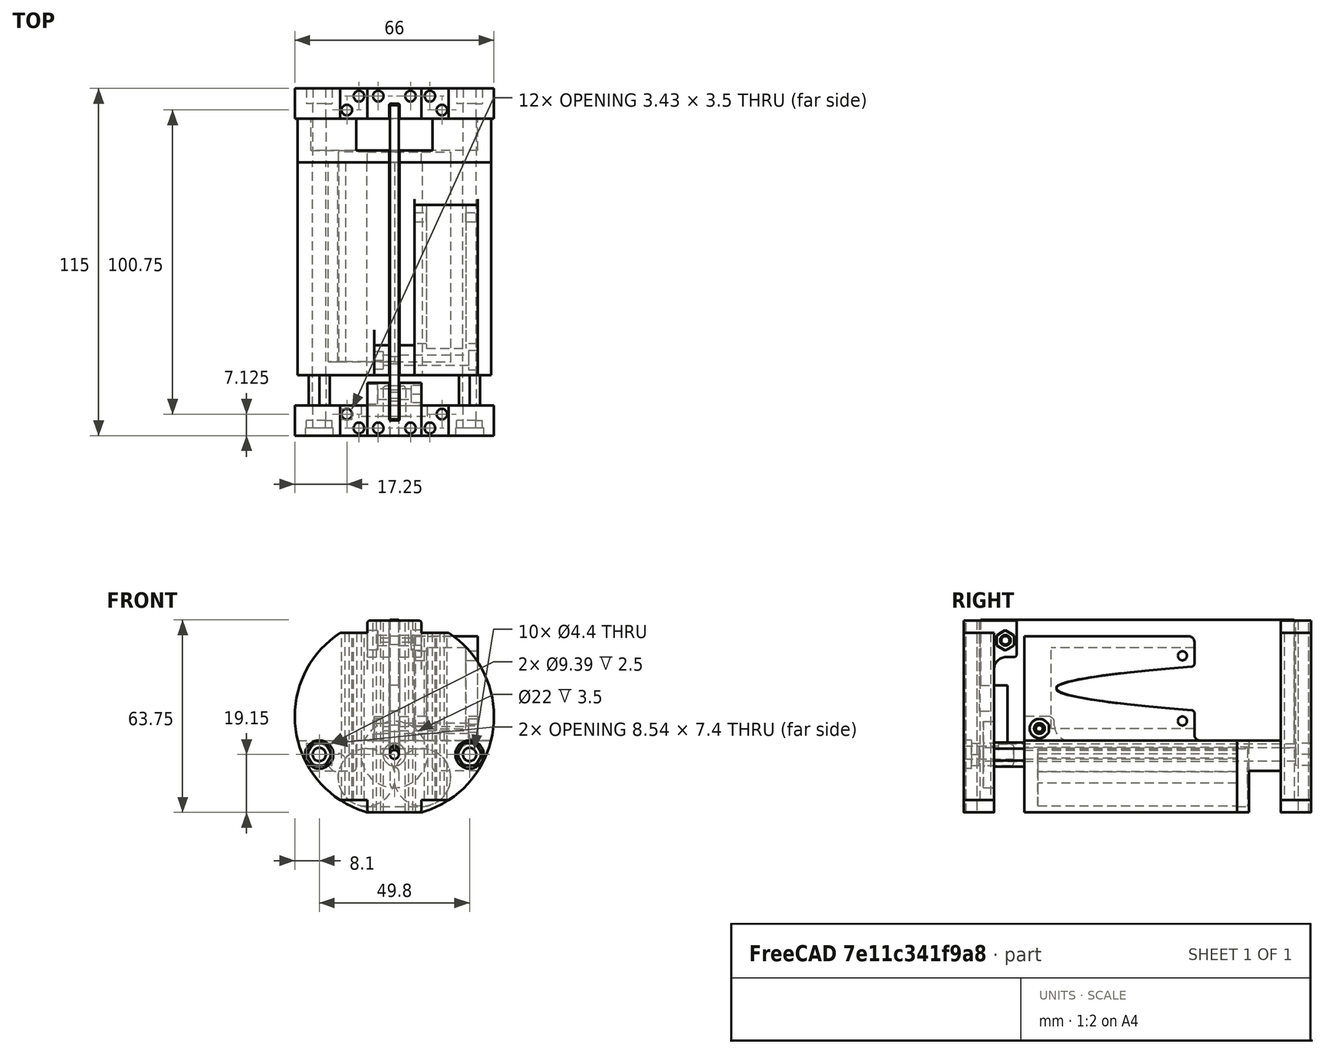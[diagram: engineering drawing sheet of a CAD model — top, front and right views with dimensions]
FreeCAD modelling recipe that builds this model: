
FCSTD DOCUMENT  (FreeCAD 0.19R24366 (Git))
Label: Corte_piezas_DEF_4
License: Creative Commons Attribution-ShareAlike
LicenseURL: http://creativecommons.org/licenses/by-sa/4.0/
objects: Sketcher::SketchObject×38, PartDesign::Pocket×24, PartDesign::Pad×14, PartDesign::Fillet×14, TechDraw::DrawViewBalloon×14, PartDesign::ShapeBinder×8, TechDraw::DrawViewPart×8, PartDesign::Body×7, PartDesign::Mirrored×5, TechDraw::DrawViewDimension×5, Part::Refine×3, TechDraw::DrawSVGTemplate×3, TechDraw::DrawPage×3, TechDraw::DrawProjGroupItem×2, Spreadsheet::Sheet×1, PartDesign::MultiTransform×1, App::DocumentObjectGroup×1, TechDraw::DrawProjGroup×1
note: 166 computed .brp shape members not serialized (recipe doc carries the construction recipe); baked Part::Feature solids carry a one-line shape summary decoded from their .brp

FEATURE [Spreadsheet::Sheet] Spreadsheet  label="Datos"
  cells = A1=Diámetro pila; B1(DiametroPila)=18.5; A2=Tolerancia; B2(tolerancia)=0.4; A3=Largo Pila; B3(largoPila)=65; A4=Separacion; B4(separacion)=1; A5=Grosor tapa; B5(grosortapa)=4.5; A6=Largo Bote; B6(LargoBote)=115; A7= Rosca pasante Diámetro; B7(roscaPasante4)=4; A8=Ancho placa electrónica; B8(anchoPlaca)=3; A9=Diámetro tornillos placa; B9(tornillosParaLaPlaca)=3; A10=GrosorGPS; B10(GPSgrosor)=12.5; A11=AnchoGPS; B11(GPSancho)=26.2; A12=AltoGPS; B12(GPSAlto)=36; A13=Ancho tuerca de 3; B13(anchoTuercaExterior)=5.4
FEATURE [Sketcher::SketchObject] Sketch  label="habitaculo_pila_antena"
  FullyConstrained = true
  MapMode = 5
  Placement = pos=(0,0,0) rot=(1,0,0;1.5708rad)
  Support = -> [XZ_Plane]
  expr: Constraints[7] = <<Datos>>.tolerancia + <<Datos>>.roscaPasante4
  expr: Constraints[2] = <<Datos>>.DiametroPila + <<Datos>>.tolerancia
  expr: Constraints[15] = <<Datos>>.DiametroPila
  sketch-geometry (13):
    g0: Circle CenterX=0 CenterY=0 CenterZ=0 NormalX=0 NormalY=0 NormalZ=1 AngleXU=0 Radius=33
    g1: LineSegment StartX=-9.25 StartY=-31.6771 StartZ=0 EndX=9.25 EndY=-31.6771 EndZ=0
    g2: LineSegment StartX=-32.0156 StartY=-8 StartZ=0 EndX=32.0156 EndY=-8 EndZ=0
    g3: ArcOfCircle CenterX=-9.25 CenterY=-20.1771 CenterZ=0 NormalX=0 NormalY=0 NormalZ=1 AngleXU=0 Radius=9.45 StartAngle=0.206102 EndAngle=2.40475
    g4: ArcOfCircle CenterX=9.25 CenterY=-20.1771 CenterZ=0 NormalX=0 NormalY=0 NormalZ=1 AngleXU=0 Radius=9.45 StartAngle=3.3477 EndAngle=9.21868
    g5: Circle CenterX=24.9 CenterY=-12.6 CenterZ=0 NormalX=0 NormalY=0 NormalZ=1 AngleXU=0 Radius=2.2
    g6: ArcOfCircle CenterX=0 CenterY=0 CenterZ=0 NormalX=0 NormalY=0 NormalZ=1 AngleXU=0 Radius=33 StartAngle=3.38646 EndAngle=4.42828
    g7: ArcOfCircle CenterX=0 CenterY=0 CenterZ=0 NormalX=0 NormalY=0 NormalZ=1 AngleXU=0 Radius=33 StartAngle=4.9965 EndAngle=6.03832
    g8: ArcOfCircle CenterX=-18.8935 CenterY=-15.243 CenterZ=0 NormalX=0 NormalY=0 NormalZ=1 AngleXU=0 Radius=3 StartAngle=0.491509 EndAngle=4.84582
    g9: ArcOfCircle CenterX=-9.25 CenterY=-20.1771 CenterZ=0 NormalX=0 NormalY=0 NormalZ=1 AngleXU=0 Radius=9.45 StartAngle=2.93258 EndAngle=6.07708
    g10: Circle CenterX=-24.9 CenterY=-12.6 CenterZ=0 NormalX=0 NormalY=0 NormalZ=1 AngleXU=0 Radius=2.2
    g11: Circle CenterX=0 CenterY=-12.6 CenterZ=0 NormalX=0 NormalY=0 NormalZ=1 AngleXU=0 Radius=1.45
    g12: LineSegment StartX=24.9 StartY=-12.6 StartZ=0 EndX=0 EndY=-12.6 EndZ=0
  constraints (38):
    c: Diameter(g0) = 66
    c: Horizontal(g1)
    c: Diameter(g3) = 18.9
    c: Equal(g3,g4)
    c: Coincident(g4,g9)
    c: Coincident(g4,g3)
    c: Coincident(g0,g-1)
    c: Diameter(g5) = 4.4
    c: Horizontal(g2)
    c: Vertical(g1,g4)
    c: Coincident(g6,g-1)
    c: Coincident(g6,g1)
    c: Coincident(g7,g6)
    c: Coincident(g7,g1)
    c: Symmetric(g4,g3,g-2)
    c: DistanceX(g3,g4) = 18.5
    c: PointOnObject(g1,g0)
    c: DistanceY(g1,g3) = 11.5
    c: DistanceY(g2,g6) = 8
    c: PointOnObject(g6,g0)
    c: Coincident(g2,g6)
    c: Coincident(g7,g2)
    c: Equal(g3,g9)
    c: Coincident(g3,g8)
    c: Coincident(g9,g8)
    c: Coincident(g3,g9)
    c: Radius(g8) = 3
    c: DistanceX(g8,g2) = -13.1222
    c: DistanceY(g8,g2) = 7.24297
    c: Symmetric(g10,g5,g-2)
    c: Equal(g10,g5)
    c: Diameter(g11) = 2.9  'Antena'
    c: Coincident(g12,g5)
    c: Coincident(g12,g11)
    c: Horizontal(g12)
    c: PointOnObject(g11,g-2)
    c: DistanceY(g5,g2) = 4.6
    c: DistanceX(g11,g5) = 24.9
FEATURE [PartDesign::Pad] Pad  label="habitaculo_Pila"
  Direction = (1,1,1)
  Length = 66
  Length2 = 100
  Midplane = true
  Placement = pos=(0,0,0) rot=(1,0,0;1.5708rad)
  Profile = -> Sketch
  Type = 0
  expr: Length = <<Datos>>.largoPila + <<Datos>>.separacion
FEATURE [PartDesign::ShapeBinder] ShapeBinder003
  Placement = pos=(0,-4.5,-1e-15) rot=(0,0,1;0rad)
  TraceSupport = false
FEATURE [Sketcher::SketchObject] Sketch022  label="Sketch_placa"
  ExternalGeometry = -> [ShapeBinder003]
  FullyConstrained = true
  Placement = pos=(0,0,-3.7e-14) rot=(0,0.707107,0.707107;3.14159rad)
  Support = -> [ShapeBinder003]
  expr: Constraints[8] = <<Datos>>.anchoPlaca
  sketch-geometry (4):
    g0: LineSegment StartX=-1.5 StartY=32 StartZ=0 EndX=1.5 EndY=32 EndZ=0
    g1: LineSegment StartX=1.5 StartY=32 StartZ=0 EndX=1.5 EndY=-9 EndZ=0
    g2: LineSegment StartX=1.5 StartY=-9 StartZ=0 EndX=-1.5 EndY=-9 EndZ=0
    g3: LineSegment StartX=-1.5 StartY=-9 StartZ=0 EndX=-1.5 EndY=32 EndZ=0
  constraints (11):
    c: Coincident(g0,g1)
    c: Coincident(g1,g2)
    c: Coincident(g2,g3)
    c: Coincident(g3,g0)
    c: Horizontal(g2)
    c: Vertical(g1)
    c: Vertical(g3)
    c: Symmetric(g0,g0,g-2)
    c: DistanceX(g0,g0) = 3
    c: DistanceY(g1,g1) = 41
    c: DistanceY(g-3,g0) = 40
FEATURE [PartDesign::Pad] Pad009  label="Placa_electrónica"
  Direction = (1,1,1)
  Length = 104
  Length2 = 100
  Midplane = true
  Placement = pos=(0,-4.5,-1e-15) rot=(0,0,1;0rad)
  Profile = -> Sketch022
  Type = 0
FEATURE [Sketcher::SketchObject] Sketch023
  ExternalGeometry = -> [Pad009]
  FullyConstrained = true
  MapMode = 5
  Placement = pos=(0,-52,5.17e-14) rot=(1,0,0;1.5708rad)
  Support = -> [Pad009]
  sketch-geometry (4):
    g0: LineSegment StartX=-1.5 StartY=-9 StartZ=0 EndX=1.5 EndY=-9 EndZ=0
    g1: LineSegment StartX=1.5 StartY=-9 StartZ=0 EndX=1.5 EndY=10.3 EndZ=0
    g2: LineSegment StartX=1.5 StartY=10.3 StartZ=0 EndX=-1.5 EndY=10.3 EndZ=0
    g3: LineSegment StartX=-1.5 StartY=10.3 StartZ=0 EndX=-1.5 EndY=-9 EndZ=0
  constraints (11):
    c: Coincident(g0,g1)
    c: Coincident(g1,g2)
    c: Coincident(g2,g3)
    c: Coincident(g3,g0)
    c: Horizontal(g0)
    c: Horizontal(g2)
    c: Vertical(g1)
    c: Vertical(g3)
    c: Coincident(g0,g-3)
    c: PointOnObject(g1,g-4)
    c: DistanceY(g1,g1) = 19.3
FEATURE [PartDesign::Pocket] Pocket011
  BaseFeature = -> Pad009
  Length = 9
  Length2 = 100
  Placement = pos=(0,-4.5,-1e-15) rot=(0,0,1;0rad)
  Profile = -> Sketch023
  Type = 0
FEATURE [PartDesign::ShapeBinder] ShapeBinder
  Placement = pos=(0,-4.5,-1e-15) rot=(0,0,1;0rad)
  TraceSupport = false
FEATURE [Sketcher::SketchObject] Sketch024  label="Forma_pasante1"
  ExternalGeometry = -> [ShapeBinder]
  FullyConstrained = true
  MapMode = 5
  Placement = pos=(0,-37.5,-1.19e-14) rot=(1,0,0;1.5708rad)
  Support = -> [ShapeBinder]
  sketch-geometry (8):
    g0: Circle CenterX=24.9 CenterY=-12.6 CenterZ=0 NormalX=0 NormalY=0 NormalZ=1 AngleXU=0 Radius=2.2
    g1: LineSegment StartX=28.3641 StartY=-14.6 StartZ=0 EndX=28.3641 EndY=-10.6 EndZ=0
    g2: LineSegment StartX=28.3641 StartY=-10.6 StartZ=0 EndX=24.9 EndY=-8.6 EndZ=0
    g3: LineSegment StartX=24.9 StartY=-8.6 StartZ=0 EndX=21.4359 EndY=-10.6 EndZ=0
    g4: LineSegment StartX=21.4359 StartY=-10.6 StartZ=0 EndX=21.4359 EndY=-14.6 EndZ=0
    g5: LineSegment StartX=21.4359 StartY=-14.6 StartZ=0 EndX=24.9 EndY=-16.6 EndZ=0
    g6: LineSegment StartX=24.9 StartY=-16.6 StartZ=0 EndX=28.3641 EndY=-14.6 EndZ=0
    g7: Circle CenterX=24.9 CenterY=-12.6 CenterZ=0 NormalX=0 NormalY=0 NormalZ=1 AngleXU=0 Radius=4
  constraints (18):
    c: Coincident(g0,g-3)
    c: Equal(g0,g-3)
    c: Coincident(g1,g2)
    c: Coincident(g2,g3)
    c: Coincident(g3,g4)
    c: Coincident(g4,g5)
    c: Coincident(g5,g6)
    c: Coincident(g6,g1)
    c: Equal(g1, g2-g6) x5
    c: PointOnObject(g1,g7)
    c: PointOnObject(g2,g7)
    c: PointOnObject(g3,g7)
    c: PointOnObject(g4,g7)
    c: PointOnObject(g5,g7)
    c: PointOnObject(g6,g7)
    c: Coincident(g7,g0)
    c: Vertical(g1)
    c: Distance(g2) = 4
FEATURE [PartDesign::Pad] Pad010
  Direction = (1,1,1)
  Length = 10
  Length2 = 100
  Placement = pos=(0,-4.5,-1e-15) rot=(0,0,1;0rad)
  Profile = -> Sketch024
  Type = 0
FEATURE [PartDesign::Body] Body004  label="Pasante1"
  Group = -> [ShapeBinder,Sketch024,Pad010]
  Origin = -> Origin004
  Tip = -> Pad010
FEATURE [PartDesign::ShapeBinder] ShapeBinder004
  Placement = pos=(0,-10,-2.2e-15) rot=(0,0,1;0rad)
  Support = -> [Pad010]
  TraceSupport = false
FEATURE [Sketcher::SketchObject] Sketch025
  ExternalGeometry = -> [ShapeBinder004]
  FullyConstrained = true
  MapMode = 5
  Placement = pos=(0,-47.5,-2.43e-14) rot=(1,0,0;1.5708rad)
  Support = -> [ShapeBinder004]
  sketch-geometry (8):
    g0: Circle CenterX=24.9 CenterY=-12.6 CenterZ=0 NormalX=0 NormalY=0 NormalZ=1 AngleXU=0 Radius=2.2
    g1: LineSegment StartX=28.3641 StartY=-10.6 StartZ=0 EndX=24.9 EndY=-8.6 EndZ=0
    g2: LineSegment StartX=24.9 StartY=-8.6 StartZ=0 EndX=21.4359 EndY=-10.6 EndZ=0
    g3: LineSegment StartX=21.4359 StartY=-10.6 StartZ=0 EndX=21.4359 EndY=-14.6 EndZ=0
    g4: LineSegment StartX=21.4359 StartY=-14.6 StartZ=0 EndX=24.9 EndY=-16.6 EndZ=0
    g5: LineSegment StartX=24.9 StartY=-16.6 StartZ=0 EndX=28.3641 EndY=-14.6 EndZ=0
    g6: LineSegment StartX=28.3641 StartY=-14.6 StartZ=0 EndX=28.3641 EndY=-10.6 EndZ=0
    g7: Circle CenterX=24.9 CenterY=-12.6 CenterZ=0 NormalX=0 NormalY=0 NormalZ=1 AngleXU=0 Radius=4
  constraints (17):
    c: Coincident(g0,g-5)
    c: PointOnObject(g-4,g0)
    c: Coincident(g1,g2)
    c: Coincident(g2,g3)
    c: Coincident(g3,g4)
    c: Coincident(g4,g5)
    c: Coincident(g5,g6)
    c: Coincident(g6,g1)
    c: Equal(g1, g2-g6) x5
    c: PointOnObject(g1,g7)
    c: PointOnObject(g2,g7)
    c: PointOnObject(g3,g7)
    c: PointOnObject(g4,g7)
    c: PointOnObject(g5,g7)
    c: PointOnObject(g6,g7)
    c: Coincident(g7,g0)
    c: Coincident(g6,g-3)
FEATURE [PartDesign::Pad] Pad011
  Direction = (1,1,1)
  Length = 10
  Length2 = 100
  Placement = pos=(0,-10,-2.2e-15) rot=(0,0,1;0rad)
  Profile = -> Sketch025
  Type = 0
FEATURE [PartDesign::Body] Body005  label="Pasante2"
  Group = -> [ShapeBinder004,Sketch025,Pad011]
  Origin = -> Origin005
  Placement = pos=(-49.8,10,1.8e-15) rot=(0,0,1;0rad)
  Tip = -> Pad011
FEATURE [PartDesign::ShapeBinder] ShapeBinder005
  Placement = pos=(0,-4.5,-1e-15) rot=(0,0,1;0rad)
  TraceSupport = false
FEATURE [Sketcher::SketchObject] Sketch026
  ExternalGeometry = -> [ShapeBinder005]
  FullyConstrained = true
  Placement = pos=(0,-47.5,0) rot=(1,0,0;1.5708rad)
  Support = -> [ShapeBinder005]
  sketch-geometry (26):
    g0: ArcOfCircle CenterX=0 CenterY=0 CenterZ=0 NormalX=0 NormalY=0 NormalZ=1 AngleXU=0 Radius=33 StartAngle=5.28932 EndAngle=7.27705
    g1: LineSegment StartX=-9 StartY=-31.749 StartZ=0 EndX=9 EndY=-31.749 EndZ=0
    g2: LineSegment StartX=-9 StartY=31.749 StartZ=0 EndX=9 EndY=31.749 EndZ=0
    g3: ArcOfCircle CenterX=0 CenterY=0 CenterZ=0 NormalX=0 NormalY=0 NormalZ=1 AngleXU=0 Radius=33 StartAngle=2.14773 EndAngle=4.13546
    g4: ArcOfCircle CenterX=0 CenterY=-12.6 CenterZ=0 NormalX=0 NormalY=0 NormalZ=1 AngleXU=0 Radius=1.45 StartAngle=3.14159 EndAngle=6.28319
    g5: ArcOfCircle CenterX=1e-16 CenterY=-11.15 CenterZ=0 NormalX=0 NormalY=0 NormalZ=1 AngleXU=0 Radius=1.45 StartAngle=0 EndAngle=3.14159
    g6: LineSegment StartX=1.45 StartY=-12.6 StartZ=0 EndX=1.45 EndY=-11.15 EndZ=0
    g7: LineSegment StartX=-1.45 StartY=-12.6 StartZ=0 EndX=-1.45 EndY=-11.15 EndZ=0
    g8: LineSegment StartX=-18 StartY=27.6586 StartZ=0 EndX=-18 EndY=-27.6586 EndZ=0
    g9: LineSegment StartX=18 StartY=27.6586 StartZ=0 EndX=18 EndY=-27.6586 EndZ=0
    g10: LineSegment StartX=27.0362 StartY=-16.3 StartZ=0 EndX=29.1724 EndY=-12.6 EndZ=0
    g11: LineSegment StartX=29.1724 StartY=-12.6 StartZ=0 EndX=27.0362 EndY=-8.9 EndZ=0
    g12: LineSegment StartX=27.0362 StartY=-8.9 StartZ=0 EndX=22.7638 EndY=-8.9 EndZ=0
    g13: LineSegment StartX=22.7638 StartY=-8.9 StartZ=0 EndX=20.6276 EndY=-12.6 EndZ=0
    g14: LineSegment StartX=20.6276 StartY=-12.6 StartZ=0 EndX=22.7638 EndY=-16.3 EndZ=0
    g15: LineSegment StartX=22.7638 StartY=-16.3 StartZ=0 EndX=27.0362 EndY=-16.3 EndZ=0
    g16: Circle CenterX=24.9 CenterY=-12.6 CenterZ=0 NormalX=0 NormalY=0 NormalZ=1 AngleXU=0 Radius=4.27239
    g17: LineSegment StartX=22.7638 StartY=-8.9 StartZ=0 EndX=29.1724 EndY=-12.6 EndZ=0
    g18: LineSegment StartX=-18 StartY=27.6586 StartZ=0 EndX=-9 EndY=27.6586 EndZ=0
    g19: LineSegment StartX=-9 StartY=31.749 StartZ=0 EndX=-9 EndY=27.6586 EndZ=0
    g20: LineSegment StartX=-18 StartY=-27.6586 StartZ=0 EndX=-9 EndY=-27.6586 EndZ=0
    g21: LineSegment StartX=-9 StartY=-31.749 StartZ=0 EndX=-9 EndY=-27.6586 EndZ=0
    g22: LineSegment StartX=9 StartY=31.749 StartZ=0 EndX=9 EndY=27.6586 EndZ=0
    g23: LineSegment StartX=18 StartY=27.6586 StartZ=0 EndX=9 EndY=27.6586 EndZ=0
    g24: LineSegment StartX=9 StartY=-31.749 StartZ=0 EndX=9 EndY=-27.6586 EndZ=0
    g25: LineSegment StartX=18 StartY=-27.6586 StartZ=0 EndX=9 EndY=-27.6586 EndZ=0
  constraints (65):
    c: Coincident(g0,g-1)
    c: Coincident(g1,g-4)
    c: PointOnObject(g2,g0)
    c: Horizontal(g2)
    c: Equal(g0,g3)
    c: Coincident(g0,g3)
    c: Tangent(g4,g7) = 1.5708
    c: Tangent(g4,g6) = -1.5708
    c: Tangent(g6,g5) = -1.5708
    c: Tangent(g7,g5) = 1.5708
    c: Vertical(g6)
    c: Equal(g4,g5)
    c: Coincident(g4,g-6)
    c: PointOnObject(g4,g-6)
    c: PointOnObject(g5,g-6)
    c: Vertical(g8)
    c: Vertical(g9)
    c: Coincident(g10,g11)
    c: Coincident(g11,g12)
    c: Coincident(g12,g13)
    c: Coincident(g13,g14)
    c: Coincident(g14,g15)
    c: Coincident(g15,g10)
    c: Equal(g10, g11-g15) x5
    c: PointOnObject(g10,g16)
    c: PointOnObject(g11,g16)
    c: PointOnObject(g12,g16)
    c: PointOnObject(g13,g16)
    c: PointOnObject(g14,g16)
    c: PointOnObject(g15,g16)
    c: Coincident(g16,g-7)
    c: Coincident(g17,g12)
    c: Coincident(g17,g10)
    c: Distance(g17) = 7.4
    c: Horizontal(g15)
    c: Coincident(g19,g2)
    c: Coincident(g19,g18)
    c: Vertical(g19)
    c: Horizontal(g18)
    c: Coincident(g3,g8)
    c: Coincident(g20,g8)
    c: Coincident(g21,g1)
    c: Coincident(g21,g20)
    c: Vertical(g21)
    c: Horizontal(g20)
    c: Coincident(g3,g8)
    c: Vertical(g22)
    c: Coincident(g23,g9)
    c: Coincident(g23,g22)
    c: Coincident(g24,g1)
    c: Vertical(g24)
    c: Coincident(g25,g9)
    c: Coincident(g25,g24)
    c: Horizontal(g25)
    c: Horizontal(g23)
    c: Coincident(g0,g9)
    c: Coincident(g0,g9)
    c: Equal(g23,g18)
    c: Equal(g20,g25)
    c: Equal(g25,g23)
    c: Coincident(g22,g2)
    c: Coincident(g18,g3)
    c: PointOnObject(g0,g-3)
    c: Coincident(g1,g-3)
    c: DistanceX(g23,g23) = 9
FEATURE [PartDesign::Pad] Pad012  label="Cuerpo_principal"
  Direction = (1,1,1)
  Length = 10
  Length2 = 100
  Placement = pos=(0,-4.5,-1e-15) rot=(0,0,1;0rad)
  Profile = -> Sketch026
  Type = 0
FEATURE [Sketcher::SketchObject] Sketch027
  ExternalGeometry = -> [Pad012]
  FullyConstrained = true
  MapMode = 5
  Placement = pos=(0,-4.5,31.749) rot=(0,0,1;0rad)
  Support = -> [Pad012]
  sketch-geometry (4):
    g0: LineSegment StartX=-1.7 StartY=-48 StartZ=0 EndX=1.7 EndY=-48 EndZ=0
    g1: LineSegment StartX=1.7 StartY=-48 StartZ=0 EndX=1.7 EndY=-43 EndZ=0
    g2: LineSegment StartX=1.7 StartY=-43 StartZ=0 EndX=-1.7 EndY=-43 EndZ=0
    g3: LineSegment StartX=-1.7 StartY=-43 StartZ=0 EndX=-1.7 EndY=-48 EndZ=0
  constraints (11):
    c: Coincident(g0,g1)
    c: Coincident(g1,g2)
    c: Coincident(g2,g3)
    c: Coincident(g3,g0)
    c: Horizontal(g0)
    c: Vertical(g1)
    c: Vertical(g3)
    c: PointOnObject(g1,g-4)
    c: Symmetric(g1,g2,g-2)
    c: DistanceX(g0,g0) = 3.4
    c: DistanceY(g1,g1) = 5
FEATURE [PartDesign::Pocket] Pocket  label="Ranura_placa"
  BaseFeature = -> Pad012
  Length = 30
  Length2 = 100
  Placement = pos=(0,-4.5,-1e-15) rot=(0,0,1;0rad)
  Profile = -> Sketch027
  Type = 0
FEATURE [Sketcher::SketchObject] Sketch028  label="SK_agujeros_pasantes_paracaidas"
  ExternalGeometry = -> [Pocket]
  FullyConstrained = true
  MapMode = 5
  Placement = pos=(0,-4.5,31.749) rot=(0,0,1;0rad)
  Support = -> [Pocket]
  sketch-geometry (14):
    g0: LineSegment StartX=-1.7 StartY=-48 StartZ=0 EndX=-9 EndY=-48 EndZ=0
    g1: LineSegment StartX=-1.7 StartY=-48 StartZ=0 EndX=-9 EndY=-53 EndZ=0
    g2: LineSegment StartX=-6.07487 StartY=-48.75 StartZ=0 EndX=-4.62513 EndY=-48.75 EndZ=0
    g3: ArcOfCircle CenterX=-5.35 CenterY=-50.5 CenterZ=0 NormalX=0 NormalY=0 NormalZ=1 AngleXU=0 Radius=1.75 StartAngle=2.35619 EndAngle=7.06858
    g4: LineSegment StartX=-6.07487 StartY=-48.75 StartZ=0 EndX=-6.58744 EndY=-49.2626 EndZ=0
    g5: LineSegment StartX=-4.11256 StartY=-49.2626 StartZ=0 EndX=-4.62513 EndY=-48.75 EndZ=0
    g6: LineSegment StartX=-6.58744 StartY=-49.2626 StartZ=0 EndX=-4.11256 EndY=-49.2626 EndZ=0
    g7: Circle CenterX=-5.35 CenterY=-50.5 CenterZ=0 NormalX=0 NormalY=0 NormalZ=1 AngleXU=0 Radius=1.75
    g8: LineSegment StartX=4.62513 StartY=-48.75 StartZ=0 EndX=6.07487 EndY=-48.75 EndZ=0
    g9: ArcOfCircle CenterX=5.35 CenterY=-50.5 CenterZ=0 NormalX=0 NormalY=0 NormalZ=1 AngleXU=0 Radius=1.75 StartAngle=2.35619 EndAngle=7.06858
    g10: LineSegment StartX=4.62513 StartY=-48.75 StartZ=0 EndX=4.11256 EndY=-49.2626 EndZ=0
    g11: LineSegment StartX=6.58744 StartY=-49.2626 StartZ=0 EndX=6.07487 EndY=-48.75 EndZ=0
    g12: LineSegment StartX=4.11256 StartY=-49.2626 StartZ=0 EndX=6.58744 EndY=-49.2626 EndZ=0
    g13: Circle CenterX=5.35 CenterY=-50.5 CenterZ=0 NormalX=0 NormalY=0 NormalZ=1 AngleXU=0 Radius=1.75
  constraints (33):
    c: Coincident(g0,g-8)
    c: PointOnObject(g0,g-3)
    c: Horizontal(g0)
    c: Coincident(g1,g0)
    c: Coincident(g1,g-3)
    c: Horizontal(g2)
    c: Coincident(g4,g2)
    c: Coincident(g5,g2)
    c: Coincident(g6,g3)
    c: Horizontal(g6)
    c: Tangent(g4,g3) = -1.5708
    c: Tangent(g5,g3) = -1.5708
    c: Angle(g6,g4) = 0.785398
    c: Diameter(g3) = 3.5
    c: Symmetric(g0,g1,g3)
    c: Coincident(g7,g3)
    c: PointOnObject(g3,g7)
    c: Tangent(g7,g2)
    c: Coincident(g3,g6)
    c: Horizontal(g8)
    c: Coincident(g10,g8)
    c: Coincident(g11,g8)
    c: Coincident(g12,g9)
    c: Horizontal(g12)
    c: Tangent(g10,g9) = -1.5708
    c: Tangent(g11,g9) = -1.5708
    c: Angle(g12,g10) = 0.785398
    c: Equal(g3,g9) = 3.5
    c: Coincident(g13,g9)
    c: PointOnObject(g9,g13)
    c: Tangent(g13,g8)
    c: Coincident(g9,g12)
    c: Symmetric(g9,g3,g-2)
FEATURE [PartDesign::Pocket] Pocket012  label="agujeros_pasantes_paracaidas"
  BaseFeature = -> Pocket
  Length = 5
  Length2 = 100
  Placement = pos=(0,-4.5,-1e-15) rot=(0,0,1;0rad)
  Profile = -> Sketch028
  Type = 1
FEATURE [Sketcher::SketchObject] Sketch029
  ExternalGeometry = -> [Pocket012]
  FullyConstrained = true
  MapMode = 5
  Placement = pos=(0,-47.5,8.5e-15) rot=(0,0.707107,0.707107;3.14159rad)
  Support = -> [Pocket012]
  sketch-geometry (2):
    g0: Circle CenterX=0 CenterY=-12.6 CenterZ=0 NormalX=0 NormalY=0 NormalZ=1 AngleXU=0 Radius=11
    g1: Circle CenterX=0 CenterY=-12.6 CenterZ=0 NormalX=0 NormalY=0 NormalZ=1 AngleXU=0 Radius=4
  constraints (4):
    c: Coincident(g0,g-3)
    c: Diameter(g0) = 22
    c: Coincident(g1,g0)
    c: Diameter(g1) = 8
FEATURE [PartDesign::Pocket] Pocket013  label="Arandela_GND"
  BaseFeature = -> Pocket012
  Length = 3.5
  Length2 = 100
  Placement = pos=(0,-4.5,-1e-15) rot=(0,0,1;0rad)
  Profile = -> Sketch029
  Type = 0
FEATURE [Sketcher::SketchObject] Sketch030
  ExternalGeometry = -> [ShapeBinder005]
  FullyConstrained = true
  MapMode = 5
  Placement = pos=(0,-57.5,1.07e-14) rot=(1,0,0;1.5708rad)
  Support = -> [Pocket013]
  sketch-geometry (15):
    g0: LineSegment StartX=27.0362 StartY=-16.3 StartZ=0 EndX=29.1724 EndY=-12.6 EndZ=0
    g1: LineSegment StartX=29.1724 StartY=-12.6 StartZ=0 EndX=27.0362 EndY=-8.9 EndZ=0
    g2: LineSegment StartX=27.0362 StartY=-8.9 StartZ=0 EndX=22.7638 EndY=-8.9 EndZ=0
    g3: LineSegment StartX=22.7638 StartY=-8.9 StartZ=0 EndX=20.6276 EndY=-12.6 EndZ=0
    g4: LineSegment StartX=20.6276 StartY=-12.6 StartZ=0 EndX=22.7638 EndY=-16.3 EndZ=0
    g5: LineSegment StartX=22.7638 StartY=-16.3 StartZ=0 EndX=27.0362 EndY=-16.3 EndZ=0
    g6: Circle CenterX=24.9 CenterY=-12.6 CenterZ=0 NormalX=0 NormalY=0 NormalZ=1 AngleXU=0 Radius=4.27239
    g7: LineSegment StartX=-22.7638 StartY=-16.3 StartZ=0 EndX=-20.6276 EndY=-12.6 EndZ=0
    g8: LineSegment StartX=-20.6276 StartY=-12.6 StartZ=0 EndX=-22.7638 EndY=-8.9 EndZ=0
    g9: LineSegment StartX=-22.7638 StartY=-8.9 StartZ=0 EndX=-27.0362 EndY=-8.9 EndZ=0
    g10: LineSegment StartX=-27.0362 StartY=-8.9 StartZ=0 EndX=-29.1724 EndY=-12.6 EndZ=0
    g11: LineSegment StartX=-29.1724 StartY=-12.6 StartZ=0 EndX=-27.0362 EndY=-16.3 EndZ=0
    g12: LineSegment StartX=-27.0362 StartY=-16.3 StartZ=0 EndX=-22.7638 EndY=-16.3 EndZ=0
    g13: Circle CenterX=-24.9 CenterY=-12.6 CenterZ=0 NormalX=0 NormalY=0 NormalZ=1 AngleXU=0 Radius=4.27239
    g14: LineSegment StartX=22.7638 StartY=-8.9 StartZ=0 EndX=29.1724 EndY=-12.6 EndZ=0
  constraints (34):
    c: Coincident(g0,g1)
    c: Coincident(g1,g2)
    c: Coincident(g2,g3)
    c: Coincident(g3,g4)
    c: Coincident(g4,g5)
    c: Coincident(g5,g0)
    c: Equal(g0, g1-g5) x5
    c: PointOnObject(g0,g6)
    c: PointOnObject(g1,g6)
    c: PointOnObject(g2,g6)
    c: PointOnObject(g3,g6)
    c: PointOnObject(g4,g6)
    c: PointOnObject(g5,g6)
    c: Coincident(g6,g-3)
    c: Coincident(g7,g8)
    c: Coincident(g8,g9)
    c: Coincident(g9,g10)
    c: Coincident(g10,g11)
    c: Coincident(g11,g12)
    c: Coincident(g12,g7)
    c: Equal(g7, g8-g12) x5
    c: PointOnObject(g7,g13)
    c: PointOnObject(g8,g13)
    c: PointOnObject(g9,g13)
    c: PointOnObject(g10,g13)
    c: PointOnObject(g11,g13)
    c: PointOnObject(g12,g13)
    c: Coincident(g13,g-4)
    c: Coincident(g14,g2)
    c: Distance(g14) = 7.4
    c: Horizontal(g5)
    c: Coincident(g14,g0)
    c: Equal(g2,g9)
    c: Horizontal(g12)
FEATURE [PartDesign::Pocket] Pocket014  label="Encastro_tuercas"
  BaseFeature = -> Pocket013
  Length = 5
  Length2 = 100
  Placement = pos=(0,-4.5,-1e-15) rot=(0,0,1;0rad)
  Profile = -> Sketch030
  Type = 0
FEATURE [Sketcher::SketchObject] Sketch031
  ExternalGeometry = -> [Pocket014]
  FullyConstrained = true
  MapMode = 5
  Placement = pos=(0,-52.5,4.51e-14) rot=(1,0,0;1.5708rad)
  Support = -> [Pocket014]
  sketch-geometry (3):
    g0: Circle CenterX=24.9 CenterY=-12.6 CenterZ=0 NormalX=0 NormalY=0 NormalZ=1 AngleXU=0 Radius=4.27239
    g1: Circle CenterX=24.9 CenterY=-12.6 CenterZ=0 NormalX=0 NormalY=0 NormalZ=1 AngleXU=0 Radius=2.2
    g2: Circle CenterX=-24.9 CenterY=-12.6 CenterZ=0 NormalX=0 NormalY=0 NormalZ=1 AngleXU=0 Radius=2.2
  constraints (7):
    c: PointOnObject(g-8,g0)
    c: PointOnObject(g-4,g0)
    c: PointOnObject(g-5,g0)
    c: Coincident(g1,g0)
    c: Diameter(g1) = 4.4
    c: Equal(g1,g2) = 4.4
    c: Symmetric(g2,g1,g-2)
FEATURE [PartDesign::Pocket] Pocket015  label="Agujeros_pasantes_tornillos"
  BaseFeature = -> Pocket014
  Length = 5
  Length2 = 100
  Placement = pos=(0,-4.5,-1e-15) rot=(0,0,1;0rad)
  Profile = -> Sketch031
  Type = 1
FEATURE [Sketcher::SketchObject] Sketch032  label="SK_agujeros_pasantes_paracaidas_2"
  ExternalGeometry = -> [Pocket015]
  FullyConstrained = true
  MapMode = 5
  Placement = pos=(0,-4.5,27.6586) rot=(0,0,1;0rad)
  Support = -> [Pocket015]
  sketch-geometry (16):
    g0: LineSegment StartX=11.0251 StartY=-48.75 StartZ=0 EndX=12.4749 EndY=-48.75 EndZ=0
    g1: ArcOfCircle CenterX=11.75 CenterY=-50.5 CenterZ=0 NormalX=0 NormalY=0 NormalZ=1 AngleXU=0 Radius=1.75 StartAngle=2.35619 EndAngle=7.06858
    g2: LineSegment StartX=11.0251 StartY=-48.75 StartZ=0 EndX=10.5126 EndY=-49.2626 EndZ=0
    g3: LineSegment StartX=12.4749 StartY=-48.75 StartZ=0 EndX=12.9874 EndY=-49.2626 EndZ=0
    g4: LineSegment StartX=10.5126 StartY=-49.2626 StartZ=0 EndX=12.9874 EndY=-49.2626 EndZ=0
    g5: LineSegment StartX=6.07487 StartY=-48.75 StartZ=0 EndX=18 EndY=-48.75 EndZ=0
    g6: LineSegment StartX=13.5 StartY=-43 StartZ=0 EndX=13.5 EndY=-53 EndZ=0
    g7: ArcOfCircle CenterX=11.75 CenterY=-50.5 CenterZ=0 NormalX=0 NormalY=0 NormalZ=1 AngleXU=0 Radius=1.75 StartAngle=1.5708 EndAngle=2.35619
    g8: LineSegment StartX=15.0251 StartY=-44.125 StartZ=0 EndX=16.4749 EndY=-44.125 EndZ=0
    g9: ArcOfCircle CenterX=15.75 CenterY=-45.875 CenterZ=0 NormalX=0 NormalY=0 NormalZ=1 AngleXU=0 Radius=1.75 StartAngle=2.35619 EndAngle=7.06858
    g10: LineSegment StartX=15.0251 StartY=-44.125 StartZ=0 EndX=14.5126 EndY=-44.6376 EndZ=0
    g11: LineSegment StartX=16.4749 StartY=-44.125 StartZ=0 EndX=16.9874 EndY=-44.6376 EndZ=0
    g12: LineSegment StartX=14.5126 StartY=-44.6376 StartZ=0 EndX=16.9874 EndY=-44.6376 EndZ=0
    g13: ArcOfCircle CenterX=15.75 CenterY=-45.875 CenterZ=0 NormalX=0 NormalY=0 NormalZ=1 AngleXU=0 Radius=1.75 StartAngle=1.57079 EndAngle=2.35619
    g14: LineSegment StartX=13.5 StartY=-43 StartZ=0 EndX=18 EndY=-48.75 EndZ=0
    g15: LineSegment StartX=13.5 StartY=-48.75 StartZ=0 EndX=18 EndY=-43 EndZ=0
  constraints (43):
    c: Diameter(g1) = 3.5
    c: Coincident(g1,g4)
    c: Horizontal(g4)
    c: Coincident(g0,g2)
    c: Horizontal(g0)
    c: Coincident(g0,g3)
    c: PointOnObject(g5,g-3)
    c: Horizontal(g5)
    c: PointOnObject(g6,g-5)
    c: Vertical(g6)
    c: Symmetric(g-4,g-6,g6)
    c: Tangent(g1,g2) = -1.5708
    c: Tangent(g3,g1) = 1.5708
    c: Coincident(g4,g1)
    c: Coincident(g7,g1)
    c: Coincident(g7,g1)
    c: Tangent(g0,g7)
    c: Angle(g4,g2) = 0.785398
    c: PointOnObject(g7,g0)
    c: Coincident(g5,g-7)
    c: Diameter(g9) = 3.5
    c: Coincident(g9,g12)
    c: Horizontal(g12)
    c: Coincident(g8,g10)
    c: Horizontal(g8)
    c: Coincident(g8,g11)
    c: Tangent(g9,g10) = -1.5708
    c: Tangent(g11,g9) = 1.5708
    c: Coincident(g12,g9)
    c: Coincident(g13,g9)
    c: Coincident(g13,g9)
    c: Tangent(g8,g13)
    c: Angle(g12,g10) = 0.785398
    c: PointOnObject(g13,g8)
    c: Coincident(g14,g6)
    c: Coincident(g14,g5)
    c: PointOnObject(g9,g14)
    c: PointOnObject(g15,g6)
    c: Coincident(g15,g-4)
    c: PointOnObject(g9,g15)
    c: PointOnObject(g15,g5)
    c: PointOnObject(g0,g5)
    c: Tangent(g1,g6)
FEATURE [PartDesign::Pocket] Pocket016  label="Agujeros_pasantes_paracaidas_2"
  BaseFeature = -> Pocket015
  Length = 5
  Length2 = 100
  Placement = pos=(0,-4.5,-1e-15) rot=(0,0,1;0rad)
  Profile = -> Sketch032
  Type = 1
FEATURE [PartDesign::Mirrored] Mirrored  label="Con_todos_agujeros_pasantes"
  BaseFeature = -> Pocket016
  MirrorPlane = -> Sketch032 [V_Axis]
  Originals = -> [Pocket016]
  Placement = pos=(0,-4.5,-1e-15) rot=(0,0,1;0rad)
FEATURE [PartDesign::Fillet] Fillet
  Base = -> Mirrored [Edge123,Edge109]
  BaseFeature = -> Mirrored
  Placement = pos=(0,-4.5,-1e-15) rot=(0,0,1;0rad)
  Radius = 0.5
  SupportTransform = false
FEATURE [PartDesign::Fillet] Fillet001
  Base = -> Fillet [Edge5,Edge9]
  BaseFeature = -> Fillet
  Placement = pos=(0,-4.5,-1e-15) rot=(0,0,1;0rad)
  Radius = 1
  SupportTransform = false
FEATURE [PartDesign::Fillet] Fillet002
  Base = -> Fillet001 [Edge114,Edge115]
  BaseFeature = -> Fillet001
  Placement = pos=(0,-4.5,-1e-15) rot=(0,0,1;0rad)
  Radius = 1
  SupportTransform = false
FEATURE [PartDesign::ShapeBinder] ShapeBinder006
  Placement = pos=(0,33,7e-15) rot=(0,0,1;0rad)
  TraceSupport = false
FEATURE [Sketcher::SketchObject] Sketch033
  ExternalGeometry = -> [ShapeBinder006]
  FullyConstrained = true
  MapMode = 5
  Placement = pos=(0,33,7e-15) rot=(0,0.707107,0.707107;3.14159rad)
  Support = -> [ShapeBinder006]
  sketch-geometry (10):
    g0: ArcOfCircle CenterX=1.2e-15 CenterY=0 CenterZ=0 NormalX=0 NormalY=0 NormalZ=1 AngleXU=0 Radius=33 StartAngle=4.98862 EndAngle=6.03832
    g1: ArcOfCircle CenterX=1.2e-15 CenterY=0 CenterZ=0 NormalX=0 NormalY=0 NormalZ=1 AngleXU=0 Radius=33 StartAngle=3.38646 EndAngle=4.43616
    g2: LineSegment StartX=-32.0156 StartY=-8 StartZ=0 EndX=32.0156 EndY=-8 EndZ=0
    g3: LineSegment StartX=9 StartY=-31.749 StartZ=0 EndX=-9 EndY=-31.749 EndZ=0
    g4: ArcOfCircle CenterX=0 CenterY=-18.3411 CenterZ=0 NormalX=0 NormalY=0 NormalZ=1 AngleXU=0 Radius=1.5 StartAngle=9e-16 EndAngle=3.14159
    g5: ArcOfCircle CenterX=0 CenterY=-22.1569 CenterZ=0 NormalX=0 NormalY=0 NormalZ=1 AngleXU=0 Radius=1.5 StartAngle=3.14159 EndAngle=6.28319
    g6: LineSegment StartX=-1.5 StartY=-18.3411 StartZ=0 EndX=-1.5 EndY=-22.1569 EndZ=0
    g7: LineSegment StartX=1.5 StartY=-18.3411 StartZ=0 EndX=1.5 EndY=-22.1569 EndZ=0
    g8: Circle CenterX=24.9 CenterY=-12.6 CenterZ=0 NormalX=0 NormalY=0 NormalZ=1 AngleXU=0 Radius=2.2
    g9: Circle CenterX=-24.9 CenterY=-12.6 CenterZ=0 NormalX=0 NormalY=0 NormalZ=1 AngleXU=0 Radius=2.2
  constraints (21):
    c: Coincident(g0,g-3)
    c: Coincident(g0,g-4)
    c: Coincident(g1,g0)
    c: Coincident(g1,g-3)
    c: Coincident(g1,g-4)
    c: Coincident(g2,g1)
    c: Coincident(g2,g0)
    c: Coincident(g3,g0)
    c: Coincident(g3,g1)
    c: Tangent(g4,g7) = 1.5708
    c: Tangent(g4,g6) = -1.5708
    c: Tangent(g6,g5) = -1.5708
    c: Tangent(g7,g5) = 1.5708
    c: Vertical(g6)
    c: Coincident(g4,g-5)
    c: Coincident(g5,g-6)
    c: Diameter(g4) = 3
    c: Coincident(g8,g-8)
    c: Equal(g8,g-7)
    c: Coincident(g9,g-7)
    c: Equal(g9,g-7)
FEATURE [PartDesign::Pad] Pad013  label="tapa_pilas"
  Direction = (1,1,1)
  Length = 4
  Length2 = 100
  Placement = pos=(0,33,7e-15) rot=(0,0,1;0rad)
  Profile = -> Sketch033
  Type = 0
FEATURE [Sketcher::SketchObject] Sketch034
  ExternalGeometry = -> [Pad013]
  FullyConstrained = true
  MapMode = 5
  Placement = pos=(0,37,8.3e-15) rot=(0,0.707107,0.707107;3.14159rad)
  Support = -> [Pad013]
  sketch-geometry (10):
    g0: ArcOfCircle CenterX=0 CenterY=0 CenterZ=0 NormalX=0 NormalY=0 NormalZ=1 AngleXU=0 Radius=33 StartAngle=3.38646 EndAngle=3.71852
    g1: LineSegment StartX=-27.6586 StartY=-18 StartZ=0 EndX=-12.6586 EndY=-18 EndZ=0
    g2: LineSegment StartX=-12.6586 StartY=-18 StartZ=0 EndX=-12.6586 EndY=-8 EndZ=0
    g3: LineSegment StartX=-32.0156 StartY=-8 StartZ=0 EndX=-12.6586 EndY=-8 EndZ=0
    g4: Circle CenterX=-24.9 CenterY=-12.6 CenterZ=0 NormalX=0 NormalY=0 NormalZ=1 AngleXU=0 Radius=2.2
    g5: ArcOfCircle CenterX=-5.1e-15 CenterY=-8.1e-15 CenterZ=0 NormalX=0 NormalY=0 NormalZ=1 AngleXU=0 Radius=33 StartAngle=5.70625 EndAngle=6.03832
    g6: LineSegment StartX=27.6586 StartY=-18 StartZ=0 EndX=12.6586 EndY=-18 EndZ=0
    g7: LineSegment StartX=12.6586 StartY=-18 StartZ=0 EndX=12.6586 EndY=-8 EndZ=0
    g8: LineSegment StartX=32.0156 StartY=-8 StartZ=0 EndX=12.6586 EndY=-8 EndZ=0
    g9: Circle CenterX=24.9 CenterY=-12.6 CenterZ=0 NormalX=0 NormalY=0 NormalZ=1 AngleXU=0 Radius=2.2
  constraints (24):
    c: Coincident(g0,g-1)
    c: Coincident(g0,g-3)
    c: Coincident(g1,g0)
    c: Horizontal(g1)
    c: PointOnObject(g2,g-3)
    c: Vertical(g2)
    c: Coincident(g2,g1)
    c: Coincident(g3,g0)
    c: Coincident(g3,g2)
    c: DistanceY(g2,g2) = 10
    c: DistanceX(g1,g1) = 15
    c: Coincident(g4,g-4)
    c: Equal(g-4,g4)
    c: Coincident(g6,g5)
    c: Coincident(g7,g6)
    c: Coincident(g8,g5)
    c: Coincident(g8,g7)
    c: Symmetric(g7,g2,g-2)
    c: Symmetric(g6,g1,g-2)
    c: Symmetric(g5,g0,g-2)
    c: Symmetric(g9,g4,g-2)
    c: Equal(g9,g4)
    c: Equal(g5,g0)
    c: Symmetric(g5,g0,g-2)
FEATURE [PartDesign::Pad] Pad014
  BaseFeature = -> Pad013
  Direction = (1,1,1)
  Length = 10.5
  Length2 = 100
  Placement = pos=(0,33,7e-15) rot=(0,0,1;0rad)
  Profile = -> Sketch034
  Type = 0
FEATURE [PartDesign::Fillet] Fillet003
  Base = -> Pad014 [Edge51,Edge48]
  BaseFeature = -> Pad014
  Placement = pos=(0,33,7e-15) rot=(0,0,1;0rad)
  Radius = 1
  SupportTransform = false
FEATURE [PartDesign::ShapeBinder] ShapeBinder007
  TraceSupport = false
FEATURE [Sketcher::SketchObject] Sketch035
  ExternalGeometry = -> [ShapeBinder007]
  FullyConstrained = true
  MapMode = 5
  Placement = pos=(0,-47.5,1.04e-14) rot=(0,0.707107,0.707107;3.14159rad)
  Support = -> [ShapeBinder007]
  sketch-geometry (14):
    g0: ArcOfCircle CenterX=0 CenterY=-1.2e-14 CenterZ=0 NormalX=0 NormalY=0 NormalZ=1 AngleXU=0 Radius=33 StartAngle=2.14773 EndAngle=4.13546
    g1: ArcOfCircle CenterX=0 CenterY=-1.2e-14 CenterZ=0 NormalX=0 NormalY=0 NormalZ=1 AngleXU=0 Radius=33 StartAngle=5.28932 EndAngle=7.27705
    g2: LineSegment StartX=-18 StartY=27.6586 StartZ=0 EndX=-9 EndY=27.6586 EndZ=0
    g3: LineSegment StartX=9 StartY=27.6586 StartZ=0 EndX=18 EndY=27.6586 EndZ=0
    g4: LineSegment StartX=-9 StartY=27.6586 StartZ=0 EndX=-9 EndY=31.749 EndZ=0
    g5: LineSegment StartX=9 StartY=27.6586 StartZ=0 EndX=9 EndY=31.749 EndZ=0
    g6: LineSegment StartX=-9 StartY=31.749 StartZ=0 EndX=9 EndY=31.749 EndZ=0
    g7: LineSegment StartX=-9 StartY=-27.6586 StartZ=0 EndX=-9 EndY=-31.749 EndZ=0
    g8: LineSegment StartX=9 StartY=-27.6586 StartZ=0 EndX=9 EndY=-31.749 EndZ=0
    g9: LineSegment StartX=9 StartY=-27.6586 StartZ=0 EndX=18 EndY=-27.6586 EndZ=0
    g10: LineSegment StartX=-18 StartY=-27.6586 StartZ=0 EndX=-9 EndY=-27.6586 EndZ=0
    g11: LineSegment StartX=-9 StartY=-31.749 StartZ=0 EndX=9 EndY=-31.749 EndZ=0
    g12: Circle CenterX=-24.9 CenterY=-12.6 CenterZ=0 NormalX=0 NormalY=0 NormalZ=1 AngleXU=0 Radius=2.2
    g13: Circle CenterX=24.9 CenterY=-12.6 CenterZ=0 NormalX=0 NormalY=0 NormalZ=1 AngleXU=0 Radius=2.2
  constraints (34):
    c: Coincident(g0,g-5)
    c: Coincident(g0,g-7)
    c: Coincident(g1,g0)
    c: Coincident(g1,g-6)
    c: Coincident(g1,g-9)
    c: Coincident(g2,g0)
    c: Coincident(g2,g-5)
    c: Coincident(g3,g-6)
    c: Coincident(g3,g1)
    c: Coincident(g4,g2)
    c: Vertical(g4)
    c: Coincident(g5,g3)
    c: Vertical(g5)
    c: Coincident(g6,g4)
    c: Coincident(g6,g5)
    c: Horizontal(g6)
    c: PointOnObject(g-3,g6)
    c: Coincident(g7,g-7)
    c: Vertical(g7)
    c: Coincident(g8,g-9)
    c: Vertical(g8)
    c: Coincident(g9,g8)
    c: Coincident(g9,g1)
    c: Coincident(g10,g0)
    c: Coincident(g10,g7)
    c: Coincident(g11,g7)
    c: Coincident(g11,g8)
    c: Horizontal(g11)
    c: PointOnObject(g-8,g11)
    c: Coincident(g12,g-10)
    c: Coincident(g13,g-11)
    c: Equal(g12,g13)
    c: Equal(g13,g-11)
    c: Coincident(g0,g-1)
FEATURE [PartDesign::Pad] Pad015
  Direction = (1,1,1)
  Length = 10
  Length2 = 100
  Profile = -> Sketch035
  Reversed = true
  Type = 0
FEATURE [Sketcher::SketchObject] Sketch036
  ExternalGeometry = -> [Pad015]
  FullyConstrained = true
  MapMode = 5
  Placement = pos=(0,-47.5,1.04e-14) rot=(0,0.707107,0.707107;3.14159rad)
  Support = -> [Pad015]
  sketch-geometry (4):
    g0: LineSegment StartX=-1.7 StartY=31.749 StartZ=0 EndX=1.7 EndY=31.749 EndZ=0
    g1: LineSegment StartX=1.7 StartY=31.749 StartZ=0 EndX=1.7 EndY=-10.351 EndZ=0
    g2: LineSegment StartX=1.7 StartY=-10.351 StartZ=0 EndX=-1.7 EndY=-10.351 EndZ=0
    g3: LineSegment StartX=-1.7 StartY=-10.351 StartZ=0 EndX=-1.7 EndY=31.749 EndZ=0
  constraints (11):
    c: Coincident(g0,g1)
    c: Coincident(g1,g2)
    c: Coincident(g2,g3)
    c: Coincident(g3,g0)
    c: Horizontal(g2)
    c: Vertical(g1)
    c: Vertical(g3)
    c: PointOnObject(g0,g-3)
    c: Symmetric(g0,g0,g-2)
    c: DistanceX(g0,g0) = 3.4
    c: DistanceY(g1,g1) = 42.1
FEATURE [PartDesign::Pocket] Pocket017
  BaseFeature = -> Pad015
  Length = 5
  Length2 = 100
  Profile = -> Sketch036
  Type = 0
FEATURE [PartDesign::Mirrored] Mirrored001
  BaseFeature = -> Pocket017
  MirrorPlane = -> Sketch028 [V_Axis]
  Originals = -> [Pocket012]
FEATURE [PartDesign::Mirrored] Mirrored002
  MirrorPlane = -> Sketch032 [V_Axis]
FEATURE [PartDesign::Mirrored] Mirrored003
  MirrorPlane = -> Sketch032 [V_Axis]
FEATURE [PartDesign::MultiTransform] MultiTransform
  BaseFeature = -> Mirrored001
  Originals = -> [Pocket016]
  Transformations = -> [Mirrored002,Mirrored003]
FEATURE [PartDesign::Mirrored] Mirrored004
  BaseFeature = -> MultiTransform
  MirrorPlane = -> Sketch030 [V_Axis]
  Originals = -> [Pocket014]
FEATURE [PartDesign::Fillet] Fillet004
  Base = -> Mirrored004 [Edge85,Edge88]
  BaseFeature = -> Mirrored004
  Radius = 0.5
  SupportTransform = false
FEATURE [PartDesign::Fillet] Fillet005
  Base = -> Fillet004 [Edge9,Edge5,Edge113,Edge114]
  BaseFeature = -> Fillet004
  Radius = 1
  SupportTransform = false
FEATURE [PartDesign::Body] Body009  label="LateralB"
  Group = -> [ShapeBinder007,Sketch035,Pad015,Sketch036,Pocket017,Mirrored001,MultiTransform,Mirrored002,Mirrored003,Mirrored004,Fillet004,Fillet005]
  Origin = -> Origin009
  Placement = pos=(0,0,0) rot=(0,0,1;3.14159rad)
  Tip = -> Fillet005
FEATURE [Sketcher::SketchObject] Sketch037
  ExternalGeometry = -> [Pad]
  FullyConstrained = true
  MapMode = 5
  Placement = pos=(0,-33,-7e-15) rot=(1,0,0;1.5708rad)
  sketch-geometry (7):
    g0: ArcOfCircle CenterX=-7e-16 CenterY=2.8e-15 CenterZ=0 NormalX=0 NormalY=0 NormalZ=1 AngleXU=0 Radius=33 StartAngle=3.38646 EndAngle=4.42828
    g1: ArcOfCircle CenterX=-7e-16 CenterY=2.8e-15 CenterZ=0 NormalX=0 NormalY=0 NormalZ=1 AngleXU=0 Radius=33 StartAngle=4.9965 EndAngle=6.03832
    g2: LineSegment StartX=-32.0156 StartY=-8 StartZ=0 EndX=32.0156 EndY=-8 EndZ=0
    g3: LineSegment StartX=9.25 StartY=-31.6771 StartZ=0 EndX=-9.25 EndY=-31.6771 EndZ=0
    g4: Circle CenterX=-24.9 CenterY=-12.6 CenterZ=0 NormalX=0 NormalY=0 NormalZ=1 AngleXU=0 Radius=2.2
    g5: Circle CenterX=0 CenterY=-12.6 CenterZ=0 NormalX=0 NormalY=0 NormalZ=1 AngleXU=0 Radius=1.45
    g6: Circle CenterX=24.9 CenterY=-12.6 CenterZ=0 NormalX=0 NormalY=0 NormalZ=1 AngleXU=0 Radius=2.2
  constraints (15):
    c: Coincident(g0,g-3)
    c: Coincident(g0,g-4)
    c: Coincident(g1,g0)
    c: Coincident(g1,g-3)
    c: Coincident(g1,g-4)
    c: Coincident(g2,g0)
    c: Coincident(g2,g1)
    c: Coincident(g3,g1)
    c: Coincident(g3,g0)
    c: Coincident(g4,g-5)
    c: Coincident(g5,g-7)
    c: Coincident(g6,g-6)
    c: Equal(g6,g-6)
    c: Equal(g5,g-7)
    c: Equal(g4,g-5)
FEATURE [PartDesign::Pad] Pad016  label="Tapa_Habitaculo_pieza"
  BaseFeature = -> Pad
  Direction = (1,1,1)
  Length = 4.5
  Length2 = 100
  Placement = pos=(0,0,0) rot=(1,0,0;1.5708rad)
  Profile = -> Sketch037
  Type = 0
  expr: Length = <<Datos>>.grosortapa
FEATURE [Sketcher::SketchObject] Sketch039  label="SK_Pieza_pasante"
  ExternalGeometry = -> [Pad016]
  FullyConstrained = true
  MapMode = 5
  Placement = pos=(0,0,-8) rot=(0,0,1;3.14159rad)
  Support = -> [Pad016]
  sketch-geometry (10):
    g0: LineSegment StartX=-6.7 StartY=37.5 StartZ=0 EndX=6.7 EndY=37.5 EndZ=0
    g1: LineSegment StartX=6.7 StartY=37.5 StartZ=0 EndX=6.7 EndY=27.5 EndZ=0
    g2: LineSegment StartX=6.7 StartY=27.5 StartZ=0 EndX=-6.7 EndY=27.5 EndZ=0
    g3: LineSegment StartX=-6.7 StartY=27.5 StartZ=0 EndX=-6.7 EndY=37.5 EndZ=0
    g4: LineSegment StartX=-1.7 StartY=33 StartZ=0 EndX=1.7 EndY=33 EndZ=0
    g5: LineSegment StartX=1.7 StartY=33 StartZ=0 EndX=1.7 EndY=0 EndZ=0
    g6: LineSegment StartX=1.7 StartY=0 StartZ=0 EndX=-1.7 EndY=0 EndZ=0
    g7: LineSegment StartX=-1.7 StartY=0 StartZ=0 EndX=-1.7 EndY=33 EndZ=0
    g8: LineSegment StartX=0 StartY=0 StartZ=0 EndX=6.7 EndY=37.5 EndZ=0
    g9: LineSegment StartX=0 StartY=0 StartZ=0 EndX=-6.7 EndY=37.5 EndZ=0
  constraints (27):
    c: Coincident(g0,g1)
    c: Coincident(g1,g2)
    c: Coincident(g2,g3)
    c: Coincident(g3,g0)
    c: Horizontal(g2)
    c: Vertical(g1)
    c: Vertical(g3)
    c: DistanceY(g3,g3) = 10
    c: DistanceX(g1,g-4) = 25.3156
    c: DistanceY(g1,g-4) = 5.5
    c: Horizontal(g0)
    c: Coincident(g4,g5)
    c: Coincident(g5,g6)
    c: Coincident(g6,g7)
    c: Coincident(g7,g4)
    c: Horizontal(g4)
    c: Vertical(g5)
    c: Vertical(g7)
    c: PointOnObject(g4,g-3)
    c: PointOnObject(g5,g-1)
    c: Symmetric(g5,g6,g-2)
    c: DistanceX(g6,g6) = 3.4
    c: Coincident(g8,g-1)
    c: Coincident(g8,g0)
    c: Coincident(g9,g-1)
    c: Coincident(g9,g0)
    c: Equal(g9,g8)
FEATURE [Sketcher::SketchObject] Sketch042
  ExternalGeometry = -> [Fillet003]
  FullyConstrained = true
  MapMode = 5
  Placement = pos=(1.4e-15,33,-8) rot=(0,0,1;0rad)
  Support = -> [Fillet003]
  expr: Constraints[10] = <<Datos>>.anchoPlaca + <<Datos>>.tolerancia
  sketch-geometry (4):
    g0: LineSegment StartX=-1.7 StartY=4 StartZ=0 EndX=1.7 EndY=4 EndZ=0
    g1: LineSegment StartX=1.7 StartY=4 StartZ=0 EndX=1.7 EndY=0 EndZ=0
    g2: LineSegment StartX=1.7 StartY=0 StartZ=0 EndX=-1.7 EndY=0 EndZ=0
    g3: LineSegment StartX=-1.7 StartY=0 StartZ=0 EndX=-1.7 EndY=4 EndZ=0
  constraints (11):
    c: Coincident(g0,g1)
    c: Coincident(g1,g2)
    c: Coincident(g2,g3)
    c: Coincident(g3,g0)
    c: Horizontal(g2)
    c: Vertical(g1)
    c: Vertical(g3)
    c: PointOnObject(g0,g-3)
    c: PointOnObject(g1,g-4)
    c: Symmetric(g0,g0,g-2)
    c: DistanceX(g0,g0) = 3.4
FEATURE [PartDesign::Pocket] Pocket020  label="Con_ranura"
  BaseFeature = -> Fillet003
  Length = 2.1
  Length2 = 100
  Placement = pos=(0,33,7e-15) rot=(0,0,1;0rad)
  Profile = -> Sketch042
  Type = 0
FEATURE [Sketcher::SketchObject] Sketch044  label="SK_algo_hundido"
  ExternalGeometry = -> [ShapeBinder006]
  FullyConstrained = true
  MapMode = 5
  Placement = pos=(0,33,7e-15) rot=(1,0,0;1.5708rad)
  Support = -> [Pocket020]
  expr: Constraints[8] = 9.199999999999999 + <<Datos>>.tolerancia
  sketch-geometry (4):
    g0: ArcOfCircle CenterX=-9 CenterY=-20.249 CenterZ=0 NormalX=0 NormalY=0 NormalZ=1 AngleXU=0 Radius=9.6 StartAngle=1.5708 EndAngle=4.71239
    g1: ArcOfCircle CenterX=9 CenterY=-20.249 CenterZ=0 NormalX=0 NormalY=0 NormalZ=1 AngleXU=0 Radius=9.6 StartAngle=4.71239 EndAngle=7.85398
    g2: LineSegment StartX=-9 StartY=-29.849 StartZ=0 EndX=9 EndY=-29.849 EndZ=0
    g3: LineSegment StartX=-9 StartY=-10.649 StartZ=0 EndX=9 EndY=-10.649 EndZ=0
  constraints (9):
    c: Tangent(g0,g3) = 1.5708
    c: Tangent(g0,g2) = -1.5708
    c: Tangent(g2,g1) = -1.5708
    c: Tangent(g3,g1) = 1.5708
    c: Horizontal(g2)
    c: Coincident(g0,g-3)
    c: Coincident(g1,g-4)
    c: Radius(g-4) = 9.2  'radio_base'
    c: Radius(g1) = 9.6
FEATURE [PartDesign::Pocket] Pocket021  label="Algo_hundido"
  BaseFeature = -> Pocket020
  Length = 3.5
  Length2 = 100
  Placement = pos=(0,33,7e-15) rot=(0,0,1;0rad)
  Profile = -> Sketch044
  Type = 0
FEATURE [PartDesign::Body] Body007  label="Tapa_Pilas"
  Group = -> [ShapeBinder006,Sketch033,Pad013,Sketch034,Pad014,Fillet003,Sketch042,Pocket020,Sketch044,Pocket021]
  Origin = -> Origin007
  Tip = -> Pocket021
FEATURE [PartDesign::Pad] Pad017  label="Pieza_atornillada"
  BaseFeature = -> Pad016
  Direction = (1,1,1)
  Length = 8
  Length2 = 100
  Placement = pos=(0,0,0) rot=(1,0,0;1.5708rad)
  Profile = -> Sketch039
  Type = 0
FEATURE [Sketcher::SketchObject] Sketch045  label="SK_caja_GPS"
  ExternalGeometry = -> [Pad017]
  FullyConstrained = true
  MapMode = 5
  Placement = pos=(0,0,-8) rot=(0,0,1;3.14159rad)
  Support = -> [Pad017]
  expr: Constraints[11] = 2 * 10 + <<Datos>>.GPSAlto + <<Datos>>.tolerancia
  expr: Constraints[9] = <<Datos>>.GPSgrosor + <<Datos>>.tolerancia + 2 * 4
  sketch-geometry (4):
    g0: LineSegment StartX=-27.6 StartY=37.5 StartZ=0 EndX=-6.7 EndY=37.5 EndZ=0
    g1: LineSegment StartX=-6.7 StartY=37.5 StartZ=0 EndX=-6.7 EndY=-18.9 EndZ=0
    g2: LineSegment StartX=-6.7 StartY=-18.9 StartZ=0 EndX=-27.6 EndY=-18.9 EndZ=0
    g3: LineSegment StartX=-27.6 StartY=-18.9 StartZ=0 EndX=-27.6 EndY=37.5 EndZ=0
  constraints (12):
    c: Coincident(g0,g1)
    c: Coincident(g1,g2)
    c: Coincident(g2,g3)
    c: Coincident(g3,g0)
    c: Horizontal(g0)
    c: Horizontal(g2)
    c: Vertical(g1)
    c: Vertical(g3)
    c: Coincident(g0,g-5)
    c: DistanceX(g0,g0) = 20.9
    c: DistanceY(g-6,g-6) = 10  'Altura_pasante'
    c: DistanceY(g3,g3) = 56.4
FEATURE [PartDesign::Pad] Pad018  label="Caja_GPS"
  BaseFeature = -> Pad017
  Direction = (1,1,1)
  Length = 34.6
  Length2 = 100
  Placement = pos=(0,0,0) rot=(1,0,0;1.5708rad)
  Profile = -> Sketch045
  Type = 0
  expr: Length = 2 * 4 + <<Datos>>.GPSancho + <<Datos>>.tolerancia
FEATURE [Sketcher::SketchObject] Sketch040  label="SK_taladro_placa"
  AttachmentOffset = pos=(11,0,0) rot=(0,0,1;0rad)
  ExternalGeometry = -> [Pad018]
  FullyConstrained = true
  MapMode = 5
  Placement = pos=(-6.7,-2.4e-15,-11) rot=(0.707107,0,-0.707107;3.14159rad)
  Support = -> [Pad018]
  sketch-geometry (7):
    g0: LineSegment StartX=-11 StartY=37.5 StartZ=0 EndX=-3 EndY=27.5 EndZ=0
    g1: LineSegment StartX=-7.72486 StartY=30.75 StartZ=0 EndX=-6.27513 EndY=30.75 EndZ=0
    g2: LineSegment StartX=-6.27513 StartY=30.75 StartZ=0 EndX=-5.76256 EndY=31.2626 EndZ=0
    g3: LineSegment StartX=-7.72486 StartY=30.75 StartZ=0 EndX=-8.23744 EndY=31.2626 EndZ=0
    g4: LineSegment StartX=-8.23744 StartY=31.2626 StartZ=0 EndX=-5.76256 EndY=31.2626 EndZ=0
    g5: ArcOfCircle CenterX=-7 CenterY=32.5 CenterZ=0 NormalX=0 NormalY=0 NormalZ=1 AngleXU=0 Radius=1.75 StartAngle=5.49779 EndAngle=10.2102
    g6: ArcOfCircle CenterX=-7 CenterY=32.5 CenterZ=0 NormalX=0 NormalY=0 NormalZ=1 AngleXU=0 Radius=1.75 StartAngle=3.92699 EndAngle=5.38713
  constraints (18):
    c: Horizontal(g1)
    c: Coincident(g2,g1)
    c: Coincident(g3,g1)
    c: Coincident(g4,g3)
    c: Coincident(g4,g2)
    c: Horizontal(g4)
    c: Coincident(g5,g4)
    c: Tangent(g5,g2) = -1.5708
    c: Diameter(g5) = 3.5
    c: Symmetric(g0,g0,g5)
    c: Coincident(g6,g5)
    c: Coincident(g6,g3)
    c: Tangent(g1,g6)
    c: Angle(g4,g2) = 0.785398
    c: Tangent(g3,g5)
    c: Coincident(g0,g-6)
    c: Coincident(g0,g-7)
    c: PointOnObject(g6,g0)
FEATURE [PartDesign::Pocket] Pocket022  label="tornillo_pasante"
  BaseFeature = -> Pad018
  Length = 5
  Length2 = 100
  Placement = pos=(0,0,0) rot=(1,0,0;1.5708rad)
  Profile = -> Sketch040
  Type = 1
FEATURE [Sketcher::SketchObject] Sketch046  label="SK_encastre_GPS"
  ExternalGeometry = -> [Pocket022]
  FullyConstrained = true
  MapMode = 5
  Placement = pos=(0,18.9,0) rot=(-1,0,0;1.5708rad)
  Support = -> [Pocket022]
  expr: Constraints[9] = <<Datos>>.GPSancho + <<Datos>>.tolerancia * 1.5
  expr: Constraints[8] = <<Datos>>.GPSgrosor + <<Datos>>.tolerancia * 1.5
  sketch-geometry (5):
    g0: LineSegment StartX=10.6 StartY=4 StartZ=0 EndX=23.7 EndY=4 EndZ=0
    g1: LineSegment StartX=23.7 StartY=4 StartZ=0 EndX=23.7 EndY=-22.8 EndZ=0
    g2: LineSegment StartX=23.7 StartY=-22.8 StartZ=0 EndX=10.6 EndY=-22.8 EndZ=0
    g3: LineSegment StartX=10.6 StartY=-22.8 StartZ=0 EndX=10.6 EndY=4 EndZ=0
    g4: LineSegment StartX=17.15 StartY=-26.6 StartZ=0 EndX=17.15 EndY=8 EndZ=0
  constraints (14):
    c: Coincident(g0,g1)
    c: Coincident(g1,g2)
    c: Coincident(g2,g3)
    c: Coincident(g3,g0)
    c: Horizontal(g0)
    c: Horizontal(g2)
    c: Vertical(g1)
    c: Vertical(g3)
    c: DistanceX(g0,g0) = 13.1
    c: DistanceY(g1,g1) = 26.8
    c: Symmetric(g1,g2,g4)
    c: PointOnObject(g4,g-3)
    c: Symmetric(g-6,g-5,g4)
    c: DistanceY(g0,g-3) = 4
FEATURE [PartDesign::Pocket] Pocket023
  BaseFeature = -> Pocket022
  Length = 47.5
  Length2 = 100
  Placement = pos=(0,0,0) rot=(1,0,0;1.5708rad)
  Profile = -> Sketch046
  Type = 0
  expr: Length = <<Datos>>.GPSAlto + 11.5
FEATURE [Sketcher::SketchObject] Sketch047  label="Forma_parabolica_SK"
  ExternalGeometry = -> [Pocket023]
  FullyConstrained = true
  MapMode = 5
  Placement = pos=(27.6,0,0) rot=(0.707107,0,0.707107;3.14159rad)
  Support = -> [Pocket023]
  expr: Constraints[1] = <<Datos>>.GPSAlto + 10
  sketch-geometry (9):
    g0: LineSegment StartX=9.3 StartY=27.1 StartZ=0 EndX=9.3 EndY=-18.9 EndZ=0
    g1: LineSegment StartX=26.6 StartY=-18.9 StartZ=0 EndX=16.6 EndY=-18.9 EndZ=0
    g2: LineSegment StartX=-8 StartY=-18.9 StartZ=0 EndX=2 EndY=-18.9 EndZ=0
    g3: ArcOfParabola CenterX=9.3 CenterY=27.1 CenterZ=0 NormalX=0 NormalY=0 NormalZ=1 Focal=0.28962 AngleXU=-1.5708 StartAngle=-7.3 EndAngle=7.3
    g4: GeomPoint X=9.3 Y=26.8104 Z=0
    g5: LineSegment StartX=9.3 StartY=27.1 StartZ=0 EndX=9.3 EndY=26.8104 EndZ=0
    g6: LineSegment StartX=2 StartY=-18.9 StartZ=0 EndX=16.6 EndY=-18.9 EndZ=0
    g7: Circle CenterX=-1.5 CenterY=-14.9 CenterZ=0 NormalX=0 NormalY=0 NormalZ=1 AngleXU=0 Radius=1.5
    g8: Circle CenterX=20.1 CenterY=-14.9 CenterZ=0 NormalX=0 NormalY=0 NormalZ=1 AngleXU=0 Radius=1.5
  constraints (22):
    c: Vertical(g0)
    c: DistanceY(g0,g0) = 46
    c: Symmetric(g-4,g-3,g0)
    c: Coincident(g1,g-4)
    c: PointOnObject(g1,g-3)
    c: Coincident(g2,g-3)
    c: PointOnObject(g2,g-3)
    c: Equal(g1,g2)
    c: DistanceX(g2,g2) = 10
    c: InternalAlignment(g4,g3)
    c: Coincident(g4,g5)
    c: Coincident(g3,g5)
    c: Coincident(g3,g0)
    c: Coincident(g3,g2)
    c: Coincident(g3,g1)
    c: Coincident(g6,g3)
    c: Coincident(g6,g3)
    c: Symmetric(g8,g7,g0)
    c: DistanceX(g8,g3) = -3.5
    c: DistanceY(g8,g3) = -4
    c: Radius(g8) = 1.5
    c: Equal(g8,g7)
FEATURE [PartDesign::Pocket] Pocket024  label="Forma_parabolica"
  BaseFeature = -> Pocket023
  Length = 0
  Length2 = 100
  Placement = pos=(0,0,0) rot=(1,0,0;1.5708rad)
  Profile = -> Sketch047
  Type = 3
  UpToFace = -> Pocket023 [Face10]
FEATURE [Sketcher::SketchObject] Sketch041  label="SK_Ranura"
  ExternalGeometry = -> [Pocket024]
  FullyConstrained = false
  MapMode = 5
  Placement = pos=(0,0,2.3e-15) rot=(0,0,1;3.14159rad)
  Support = -> [Pocket024]
  expr: Constraints[8] = <<Datos>>.anchoPlaca + <<Datos>>.tolerancia
  sketch-geometry (4):
    g0: LineSegment StartX=-1.7 StartY=37.5 StartZ=0 EndX=1.7 EndY=37.5 EndZ=0
    g1: LineSegment StartX=1.7 StartY=37.5 StartZ=0 EndX=1.7 EndY=-40.4029 EndZ=0
    g2: LineSegment StartX=1.7 StartY=-40.4029 StartZ=0 EndX=-1.7 EndY=-40.4029 EndZ=0
    g3: LineSegment StartX=-1.7 StartY=-40.4029 StartZ=0 EndX=-1.7 EndY=37.5 EndZ=0
  constraints (10):
    c: Coincident(g0,g1)
    c: Coincident(g1,g2)
    c: Coincident(g2,g3)
    c: Coincident(g3,g0)
    c: Horizontal(g2)
    c: Vertical(g1)
    c: Vertical(g3)
    c: Symmetric(g0,g0,g-2)
    c: DistanceX(g0,g0) = 3.4
    c: PointOnObject(g0,g-3)
FEATURE [PartDesign::Pocket] Pocket025  label="Ranura_placa_en_habitaculo"
  BaseFeature = -> Pocket024
  Length = 10.3
  Length2 = 100
  Placement = pos=(0,0,0) rot=(1,0,0;1.5708rad)
  Profile = -> Sketch041
  Type = 0
FEATURE [Sketcher::SketchObject] Sketch048  label="SK_protuberancia"
  ExternalGeometry = -> [Fillet002]
  FullyConstrained = true
  MapMode = 5
  Placement = pos=(-1.02e-14,-51,1.62e-14) rot=(0,0.707107,0.707107;3.14159rad)
  Support = -> [Fillet002]
  sketch-geometry (5):
    g0: Circle CenterX=-1.02e-14 CenterY=-12.6 CenterZ=0 NormalX=0 NormalY=0 NormalZ=1 AngleXU=0 Radius=3.75
    g1: ArcOfCircle CenterX=-1.03e-14 CenterY=-11.15 CenterZ=0 NormalX=0 NormalY=0 NormalZ=1 AngleXU=0 Radius=1.45 StartAngle=1.2252e-12 EndAngle=3.14159
    g2: ArcOfCircle CenterX=-1.02e-14 CenterY=-12.6 CenterZ=0 NormalX=0 NormalY=0 NormalZ=1 AngleXU=0 Radius=1.45 StartAngle=3.14159 EndAngle=6.28319
    g3: LineSegment StartX=-1.45 StartY=-11.15 StartZ=0 EndX=-1.45 EndY=-12.6 EndZ=0
    g4: LineSegment StartX=1.45 StartY=-11.15 StartZ=0 EndX=1.45 EndY=-12.6 EndZ=0
  constraints (9):
    c: Coincident(g0,g-4)
    c: Diameter(g0) = 7.5
    c: Tangent(g1,g4) = 1.5708
    c: Tangent(g1,g3) = -1.5708
    c: Tangent(g3,g2) = -1.5708
    c: Tangent(g4,g2) = 1.5708
    c: Coincident(g1,g-5)
    c: Coincident(g2,g0)
    c: Coincident(g1,g-5)
FEATURE [PartDesign::Pad] Pad019  label="Protuberancia_antena"
  BaseFeature = -> Fillet002
  Direction = (1,1,1)
  Length = 5
  Length2 = 100
  Placement = pos=(0,-4.5,-1e-15) rot=(0,0,1;0rad)
  Profile = -> Sketch048
  Type = 0
FEATURE [Sketcher::SketchObject] Sketch049  label="SK_Acomodo_tuercas"
  ExternalGeometry = -> [Pad019]
  FullyConstrained = true
  MapMode = 5
  Placement = pos=(0,-57.5,1.07e-14) rot=(1,0,0;1.5708rad)
  Support = -> [Pad019]
  expr: Constraints[7] = <<Datos>>.tolerancia
  sketch-geometry (4):
    g0: Circle CenterX=-24.9 CenterY=-12.6 CenterZ=0 NormalX=0 NormalY=0 NormalZ=1 AngleXU=0 Radius=4.69355
    g1: Circle CenterX=24.9 CenterY=-12.6 CenterZ=0 NormalX=0 NormalY=0 NormalZ=1 AngleXU=0 Radius=4.69355
    g2: LineSegment StartX=-24.9 StartY=-12.6 StartZ=0 EndX=-29.4448 EndY=-14.8998 EndZ=0
    g3: GeomPoint X=-29.0879 Y=-14.7192 Z=0
  constraints (9):
    c: Coincident(g0,g-3)
    c: Equal(g1,g0)
    c: PointOnObject(g2,g-6)
    c: Coincident(g2,g0)
    c: Perpendicular(g-6,g2)
    c: PointOnObject(g3,g0)
    c: PointOnObject(g3,g2)
    c: Distance(g2,g3) = 0.4
    c: Coincident(g1,g-4)
FEATURE [PartDesign::Pocket] Pocket026  label="Acomodo_tuercas"
  BaseFeature = -> Pad019
  Length = 2.5
  Length2 = 100
  Placement = pos=(0,-4.5,-1e-15) rot=(0,0,1;0rad)
  Profile = -> Sketch049
  Type = 0
FEATURE [PartDesign::Fillet] Fillet012
  Base = -> Pocket026 [Edge160]
  BaseFeature = -> Pocket026
  Placement = pos=(0,-4.5,-1e-15) rot=(0,0,1;0rad)
  Radius = 0.5
  SupportTransform = false
FEATURE [Sketcher::SketchObject] Sketch050
  ExternalGeometry = -> [Pad019]
  FullyConstrained = true
  MapMode = 5
  Placement = pos=(0,-46,-1e-15) rot=(0,0.707107,0.707107;3.14159rad)
  Support = -> [Pad019]
  sketch-geometry (4):
    g0: ArcOfCircle CenterX=-1.1e-15 CenterY=-12.6 CenterZ=0 NormalX=0 NormalY=0 NormalZ=1 AngleXU=0 Radius=3.75 StartAngle=1.96781 EndAngle=7.45697
    g1: LineSegment StartX=-1.45 StartY=-12.6 StartZ=0 EndX=-1.45 EndY=-9.14168 EndZ=0
    g2: LineSegment StartX=1.45 StartY=-12.6 StartZ=0 EndX=1.45 EndY=-9.14168 EndZ=0
    g3: ArcOfCircle CenterX=-1.1e-15 CenterY=-12.6 CenterZ=0 NormalX=0 NormalY=0 NormalZ=1 AngleXU=0 Radius=1.45 StartAngle=3.14159 EndAngle=6.28319
  constraints (11):
    c: Coincident(g0,g-4)
    c: PointOnObject(g0,g-3)
    c: Coincident(g1,g-4)
    c: Coincident(g1,g0)
    c: Coincident(g2,g-4)
    c: Coincident(g2,g0)
    c: Vertical(g2)
    c: Vertical(g1)
    c: Coincident(g3,g0)
    c: Coincident(g3,g2)
    c: Coincident(g3,g1)
FEATURE [PartDesign::Pad] Pad020  label="Acomodo_tuerca"
  BaseFeature = -> Fillet012
  Direction = (1,1,1)
  Length = 5
  Length2 = 100
  Placement = pos=(0,-4.5,-1e-15) rot=(0,0,1;0rad)
  Profile = -> Sketch050
  Type = 0
FEATURE [PartDesign::Fillet] Fillet013  label="Pieza_lateral_A"
  Base = -> Pad020 [Edge35]
  BaseFeature = -> Pad020
  Placement = pos=(0,-4.5,-1e-15) rot=(0,0,1;0rad)
  Radius = 1
  SupportTransform = false
FEATURE [Sketcher::SketchObject] Sketch051  label="SK_Tuerca"
  ExternalGeometry = -> [Pocket025]
  FullyConstrained = true
  MapMode = 5
  Placement = pos=(-6.7,0,0) rot=(0.707107,0,-0.707107;3.14159rad)
  Support = -> [Pocket025]
  expr: Constraints[19] = <<Datos>>.anchoTuercaExterior + <<Datos>>.tolerancia
  sketch-geometry (7):
    g0: LineSegment StartX=5.67432 StartY=29.6 StartZ=0 EndX=7.34863 EndY=32.5 EndZ=0
    g1: LineSegment StartX=7.34863 StartY=32.5 StartZ=0 EndX=5.67432 EndY=35.4 EndZ=0
    g2: LineSegment StartX=5.67432 StartY=35.4 StartZ=0 EndX=2.32568 EndY=35.4 EndZ=0
    g3: LineSegment StartX=2.32568 StartY=35.4 StartZ=0 EndX=0.651368 EndY=32.5 EndZ=0
    g4: LineSegment StartX=0.651368 StartY=32.5 StartZ=0 EndX=2.32568 EndY=29.6 EndZ=0
    g5: LineSegment StartX=2.32568 StartY=29.6 StartZ=0 EndX=5.67432 EndY=29.6 EndZ=0
    g6: Circle CenterX=4 CenterY=32.5 CenterZ=0 NormalX=0 NormalY=0 NormalZ=1 AngleXU=0 Radius=3.34863
  constraints (16):
    c: Coincident(g0,g1)
    c: Coincident(g1,g2)
    c: Coincident(g2,g3)
    c: Coincident(g3,g4)
    c: Coincident(g4,g5)
    c: Coincident(g5,g0)
    c: Equal(g0, g1-g5) x5
    c: PointOnObject(g0,g6)
    c: PointOnObject(g1,g6)
    c: PointOnObject(g2,g6)
    c: PointOnObject(g3,g6)
    c: PointOnObject(g4,g6)
    c: PointOnObject(g5,g6)
    c: Coincident(g6,g-3)
    c: Horizontal(g2)
    c: Distance(g2,g0) = 5.8
FEATURE [PartDesign::Pocket] Pocket027  label="Tuerca_encrastada"
  BaseFeature = -> Pocket025
  Length = 3
  Length2 = 100
  Placement = pos=(0,0,0) rot=(1,0,0;1.5708rad)
  Profile = -> Sketch051
  Type = 0
FEATURE [PartDesign::Fillet] Fillet014
  Base = -> Pocket027 [Edge7,Edge68]
  BaseFeature = -> Pocket027
  Placement = pos=(0,0,0) rot=(1,0,0;1.5708rad)
  Radius = 5
  SupportTransform = false
FEATURE [PartDesign::Fillet] Fillet015
  Base = -> Fillet014 [Edge48,Edge130]
  BaseFeature = -> Fillet014
  Placement = pos=(0,0,0) rot=(1,0,0;1.5708rad)
  Radius = 2
  SupportTransform = false
FEATURE [PartDesign::Fillet] Fillet016
  Base = -> Fillet015 [Edge86,Edge163]
  BaseFeature = -> Fillet015
  Placement = pos=(0,0,0) rot=(1,0,0;1.5708rad)
  Radius = 2
  SupportTransform = false
FEATURE [PartDesign::Fillet] Fillet017
  Base = -> Fillet016 [Edge69,Edge71,Edge75,Edge77]
  BaseFeature = -> Fillet016
  Placement = pos=(0,0,0) rot=(1,0,0;1.5708rad)
  Radius = 1
  SupportTransform = false
FEATURE [Sketcher::SketchObject] Sketch052  label="SK_CABEZA_TORNILLO"
  ExternalGeometry = -> [Fillet017]
  FullyConstrained = true
  MapMode = 5
  Placement = pos=(27.6,0,0) rot=(0.707107,0,0.707107;3.14159rad)
  Support = -> [Fillet017]
  expr: Constraints[1] = 6 + <<Datos>>.tolerancia
  sketch-geometry (9):
    g0: Circle CenterX=-4 CenterY=32.5 CenterZ=0 NormalX=0 NormalY=0 NormalZ=1 AngleXU=0 Radius=3.2
    g1: LineSegment StartX=-6.26274 StartY=30.2373 StartZ=0 EndX=-5.32548 EndY=29.3 EndZ=0
    g2: LineSegment StartX=-1.73726 StartY=30.2373 StartZ=0 EndX=-2.67452 EndY=29.3 EndZ=0
    g3: LineSegment StartX=-6.26274 StartY=30.2373 StartZ=0 EndX=-1.73726 EndY=30.2373 EndZ=0
    g4: LineSegment StartX=-5.32548 StartY=29.3 StartZ=0 EndX=-2.67452 EndY=29.3 EndZ=0
    g5: ArcOfCircle CenterX=-4 CenterY=32.5 CenterZ=0 NormalX=0 NormalY=0 NormalZ=1 AngleXU=0 Radius=3.2 StartAngle=5.49779 EndAngle=10.2102
    g6: LineSegment StartX=-1.73726 StartY=30.2373 StartZ=0 EndX=-2.67452 EndY=29.3 EndZ=0
    g7: LineSegment StartX=-2.67452 StartY=29.3 StartZ=0 EndX=-5.32548 EndY=29.3 EndZ=0
    g8: LineSegment StartX=-5.32548 StartY=29.3 StartZ=0 EndX=-6.26275 EndY=30.2373 EndZ=0
  constraints (23):
    c: Coincident(g0,g-3)
    c: Diameter(g0) = 6.4
    c: PointOnObject(g1,g0)
    c: PointOnObject(g2,g0)
    c: Coincident(g3,g1)
    c: Coincident(g3,g2)
    c: Horizontal(g3)
    c: Tangent(g1,g0)
    c: Tangent(g2,g0)
    c: Coincident(g4,g1)
    c: Coincident(g4,g2)
    c: Horizontal(g4)
    c: Tangent(g4,g0)
    c: Angle(g4,g1) = 2.35619
    c: Coincident(g5,g0)
    c: Coincident(g5,g2)
    c: Coincident(g6,g5)
    c: Coincident(g6,g2)
    c: Coincident(g7,g6)
    c: Coincident(g7,g1)
    c: Coincident(g8,g7)
    c: Coincident(g8,g5)
    c: Tangent(g8,g0)
FEATURE [PartDesign::Pocket] Pocket028  label="Con_Cabeza_tornillo"
  BaseFeature = -> Fillet017
  Length = 3
  Length2 = 100
  Placement = pos=(0,0,0) rot=(1,0,0;1.5708rad)
  Profile = -> Sketch052
  Type = 0
FEATURE [Sketcher::SketchObject] Sketch053  label="Pieza_tornillo_SK"
  ExternalGeometry = -> [Fillet013]
  FullyConstrained = true
  MapMode = 5
  Placement = pos=(0,-47.5,8.5e-15) rot=(0,0.707107,0.707107;3.14159rad)
  Support = -> [Fillet013]
  sketch-geometry (6):
    g0: LineSegment StartX=-8 StartY=31.749 StartZ=0 EndX=8 EndY=31.749 EndZ=0
    g1: LineSegment StartX=9 StartY=30.749 StartZ=0 EndX=9 EndY=19.6586 EndZ=0
    g2: LineSegment StartX=9 StartY=19.6586 StartZ=0 EndX=-9 EndY=19.6586 EndZ=0
    g3: LineSegment StartX=-9 StartY=19.6586 StartZ=0 EndX=-9 EndY=30.749 EndZ=0
    g4: ArcOfCircle CenterX=-8 CenterY=30.749 CenterZ=0 NormalX=0 NormalY=0 NormalZ=1 AngleXU=0 Radius=1 StartAngle=1.5708 EndAngle=3.14159
    g5: ArcOfCircle CenterX=8 CenterY=30.749 CenterZ=0 NormalX=0 NormalY=0 NormalZ=1 AngleXU=0 Radius=1 StartAngle=-1.8e-15 EndAngle=1.5708
  constraints (14):
    c: Coincident(g1,g2)
    c: Coincident(g2,g3)
    c: Horizontal(g2)
    c: Vertical(g1)
    c: Vertical(g3)
    c: PointOnObject(g-3,g3)
    c: PointOnObject(g-6,g1)
    c: Tangent(g0,g4) = 1.5708
    c: Tangent(g3,g4) = 1.5708
    c: Tangent(g0,g5) = 1.5708
    c: Tangent(g1,g5) = 1.5708
    c: Coincident(g0,g-5)
    c: Coincident(g0,g-4)
    c: DistanceY(g1,g-6) = 8
FEATURE [PartDesign::Pad] Pad021  label="Pieza_tornillo"
  BaseFeature = -> Fillet013
  Direction = (1,1,1)
  Length = 7.5
  Length2 = 100
  Placement = pos=(0,-4.5,-1e-15) rot=(0,0,1;0rad)
  Profile = -> Sketch053
  Type = 0
FEATURE [PartDesign::Pocket] Pocket029  label="Encastro_tuercas001"
  BaseFeature = -> Pad021
  Length = 5
  Length2 = 100
  Placement = pos=(0,-4.5,-1e-15) rot=(0,0,1;0rad)
  Profile = -> Sketch030
  Type = 0
FEATURE [Sketcher::SketchObject] Sketch054  label="SK_tornillo_atraviesa"
  ExternalGeometry = -> [Pocket029]
  FullyConstrained = true
  MapMode = 5
  Placement = pos=(9,-4.5,-1e-15) rot=(0.57735,0.57735,0.57735;2.0944rad)
  Support = -> [Pocket029]
  sketch-geometry (7):
    g0: LineSegment StartX=-43 StartY=30.749 StartZ=0 EndX=-35.5 EndY=19.6586 EndZ=0
    g1: LineSegment StartX=-35.5 StartY=30.749 StartZ=0 EndX=-43 EndY=19.6586 EndZ=0
    g2: LineSegment StartX=-38.0126 StartY=26.4413 StartZ=0 EndX=-38.0126 EndY=23.9664 EndZ=0
    g3: ArcOfCircle CenterX=-39.25 CenterY=25.2038 CenterZ=0 NormalX=0 NormalY=0 NormalZ=1 AngleXU=0 Radius=1.75 StartAngle=0.785398 EndAngle=5.49779
    g4: LineSegment StartX=-37.5 StartY=25.9287 StartZ=0 EndX=-37.5 EndY=24.479 EndZ=0
    g5: LineSegment StartX=-38.0126 StartY=23.9664 StartZ=0 EndX=-37.5 EndY=24.479 EndZ=0
    g6: LineSegment StartX=-37.5 StartY=25.9287 StartZ=0 EndX=-38.0126 EndY=26.4413 EndZ=0
  constraints (17):
    c: Coincident(g0,g-4)
    c: Coincident(g0,g-3)
    c: Coincident(g1,g-4)
    c: Coincident(g1,g-5)
    c: Vertical(g2)
    c: PointOnObject(g3,g0)
    c: PointOnObject(g3,g1)
    c: Diameter(g3) = 3.5
    c: Coincident(g5,g4)
    c: Vertical(g4)
    c: Tangent(g5,g3) = -1.5708
    c: Coincident(g3,g2)
    c: Angle(g5,g2) = 0.785398
    c: Coincident(g6,g4)
    c: Tangent(g6,g3) = -1.5708
    c: Coincident(g3,g2)
    c: Tangent(g4,g3)
FEATURE [PartDesign::Pocket] Pocket030  label="Tornillo_atraviesa"
  BaseFeature = -> Pocket029
  Length = 5
  Length2 = 100
  Placement = pos=(0,-4.5,-1e-15) rot=(0,0,1;0rad)
  Profile = -> Sketch054
  Type = 2
FEATURE [Sketcher::SketchObject] Sketch055
  ExternalGeometry = -> [Pocket030]
  FullyConstrained = false
  MapMode = 5
  Placement = pos=(0,-47.5,8.5e-15) rot=(0,0.707107,0.707107;3.14159rad)
  Support = -> [Pocket030]
  sketch-geometry (4):
    g0: LineSegment StartX=-1.7 StartY=1.74902 StartZ=0 EndX=1.7 EndY=1.74902 EndZ=0
    g1: LineSegment StartX=1.7 StartY=1.74902 StartZ=0 EndX=1.7 EndY=45.8594 EndZ=0
    g2: LineSegment StartX=1.7 StartY=45.8594 StartZ=0 EndX=-1.7 EndY=45.8594 EndZ=0
    g3: LineSegment StartX=-1.7 StartY=45.8594 StartZ=0 EndX=-1.7 EndY=1.74902 EndZ=0
  constraints (9):
    c: Coincident(g0,g1)
    c: Coincident(g1,g2)
    c: Coincident(g2,g3)
    c: Coincident(g3,g0)
    c: Horizontal(g2)
    c: Vertical(g1)
    c: Vertical(g3)
    c: Coincident(g0,g-4)
    c: Coincident(g0,g-5)
FEATURE [PartDesign::Pocket] Pocket031  label="Ampliacion_ranura"
  BaseFeature = -> Pocket030
  Length = 10
  Length2 = 100
  Placement = pos=(0,-4.5,-1e-15) rot=(0,0,1;0rad)
  Profile = -> Sketch055
  Reversed = true
  Type = 0
FEATURE [Sketcher::SketchObject] Sketch056  label="SK_empotra_tuerca"
  ExternalGeometry = -> [Pocket031]
  FullyConstrained = true
  MapMode = 5
  Placement = pos=(9,-4.5,-1e-15) rot=(0.57735,0.57735,0.57735;2.0944rad)
  Support = -> [Pocket031]
  expr: Constraints[19] = 5.4 + <<Datos>>.tolerancia
  sketch-geometry (7):
    g0: LineSegment StartX=-36.35 StartY=23.5295 StartZ=0 EndX=-36.35 EndY=26.8781 EndZ=0
    g1: LineSegment StartX=-36.35 StartY=26.8781 StartZ=0 EndX=-39.25 EndY=28.5525 EndZ=0
    g2: LineSegment StartX=-39.25 StartY=28.5525 StartZ=0 EndX=-42.15 EndY=26.8781 EndZ=0
    g3: LineSegment StartX=-42.15 StartY=26.8781 StartZ=0 EndX=-42.15 EndY=23.5295 EndZ=0
    g4: LineSegment StartX=-42.15 StartY=23.5295 StartZ=0 EndX=-39.25 EndY=21.8552 EndZ=0
    g5: LineSegment StartX=-39.25 StartY=21.8552 StartZ=0 EndX=-36.35 EndY=23.5295 EndZ=0
    g6: Circle CenterX=-39.25 CenterY=25.2038 CenterZ=0 NormalX=0 NormalY=0 NormalZ=1 AngleXU=0 Radius=3.34863
  constraints (16):
    c: Coincident(g0,g1)
    c: Coincident(g1,g2)
    c: Coincident(g2,g3)
    c: Coincident(g3,g4)
    c: Coincident(g4,g5)
    c: Coincident(g5,g0)
    c: Equal(g0, g1-g5) x5
    c: PointOnObject(g0,g6)
    c: PointOnObject(g1,g6)
    c: PointOnObject(g2,g6)
    c: PointOnObject(g3,g6)
    c: PointOnObject(g4,g6)
    c: PointOnObject(g5,g6)
    c: Coincident(g6,g-3)
    c: Vertical(g0)
    c: DistanceX(g2,g0) = 5.8
FEATURE [PartDesign::Pocket] Pocket032  label="Empotrar_tuerca_pequeña"
  BaseFeature = -> Pocket031
  Length = 3.5
  Length2 = 100
  Placement = pos=(0,-4.5,-1e-15) rot=(0,0,1;0rad)
  Profile = -> Sketch056
  Type = 0
FEATURE [Sketcher::SketchObject] Sketch057  label="SK_cabeza_tornillo"
  ExternalGeometry = -> [Pocket032]
  FullyConstrained = true
  MapMode = 5
  Placement = pos=(-9,-4.5,-1e-15) rot=(0.57735,-0.57735,-0.57735;2.0944rad)
  Support = -> [Pocket032]
  expr: Constraints[1] = 6 + <<Datos>>.tolerancia
  sketch-geometry (1):
    g0: Circle CenterX=39.25 CenterY=25.2038 CenterZ=0 NormalX=0 NormalY=0 NormalZ=1 AngleXU=0 Radius=3.2
  constraints (2):
    c: Coincident(g0,g-3)
    c: Diameter(g0) = 6.4
FEATURE [PartDesign::Pocket] Pocket033  label="Cabeza_tornillo"
  BaseFeature = -> Pocket032
  Length = 3.5
  Length2 = 100
  Placement = pos=(0,-4.5,-1e-15) rot=(0,0,1;0rad)
  Profile = -> Sketch057
  Type = 0
FEATURE [PartDesign::Fillet] Fillet018
  Base = -> Pocket033 [Edge153,Edge157]
  BaseFeature = -> Pocket033
  Placement = pos=(0,-4.5,-1e-15) rot=(0,0,1;0rad)
  Radius = 4
  SupportTransform = false
FEATURE [PartDesign::Fillet] Fillet019
  Base = -> Fillet018 [Edge168,Edge151]
  BaseFeature = -> Fillet018
  Placement = pos=(0,-4.5,-1e-15) rot=(0,0,1;0rad)
  Radius = 1
  SupportTransform = false
FEATURE [Part::Refine] Body007003  label="Tapa_Pilas001"
  Source = -> Body007
FEATURE [Sketcher::SketchObject] Sketch058  label="Taladro_posicional_1"
  FullyConstrained = false
  MapMode = 5
  Placement = pos=(-1.5,-4.5,-1e-15) rot=(0.57735,-0.57735,-0.57735;2.0944rad)
  Support = -> [Pocket011]
  sketch-geometry (1):
    g0: Circle CenterX=28 CenterY=-4 CenterZ=0 NormalX=0 NormalY=0 NormalZ=1 AngleXU=0 Radius=1.1153
FEATURE [PartDesign::Body] Body  label="Habitaculo_Pila"
  Group = -> [Sketch,Pad,Sketch037,Pad016,Sketch039,Sketch040,Sketch041,Pad017,Sketch045,Pad018,Sketch046,Pocket022,Pocket023,Sketch047,Pocket024,Pocket025,Sketch051,Pocket027,Fillet014,Fillet015,Fillet016,Fillet017,Sketch052,Pocket028,Sketch058]
  Origin = -> Origin
  Tip = -> Pocket028
FEATURE [Part::Refine] Body007002  label="Habitaculo_Pila001"
  Source = -> Body
FEATURE [PartDesign::ShapeBinder] ShapeBinder008  label="Taladro_posicional_002"
  Placement = pos=(-1.5,-4.5,-1e-15) rot=(0.57735,-0.57735,-0.57735;2.0944rad)
  Support = -> [Sketch058]
  TraceSupport = false
FEATURE [PartDesign::Pocket] Pocket034
  BaseFeature = -> Pocket011
  Length = 5
  Length2 = 100
  Placement = pos=(0,-4.5,-1e-15) rot=(0,0,1;0rad)
  Profile = -> ShapeBinder008
  Type = 0
FEATURE [Sketcher::SketchObject] Sketch059  label="Taladro_posicional_2"
  ExternalGeometry = -> [Fillet019]
  FullyConstrained = false
  MapMode = 5
  Placement = pos=(-5.5,-4.5,-1e-15) rot=(0.57735,-0.57735,-0.57735;2.0944rad)
  Support = -> [Fillet019]
  sketch-geometry (1):
    g0: Circle CenterX=39.25 CenterY=25.2038 CenterZ=0 NormalX=0 NormalY=0 NormalZ=1 AngleXU=0 Radius=1.38254
  constraints (1):
    c: Coincident(g0,g-3)
FEATURE [PartDesign::Body] Body006  label="LateralA"
  Group = -> [ShapeBinder005,Sketch026,Pad012,Sketch027,Pocket,Sketch028,Pocket012,Sketch029,Pocket013,Sketch030,Pocket014,Sketch031,Pocket015,Sketch032,Pocket016,Mirrored,Fillet,Fillet001,Fillet002,Sketch048,Pad019,Sketch049,Pocket026,Fillet012,Sketch050,Pad020,Fillet013,Sketch053,Pad021,Pocket029,Sketch054,Pocket030,Sketch055,Pocket031,Sketch056,Pocket032,Sketch057,Pocket033,Fillet018,Fillet019,Sketch059]
  Origin = -> Origin006
  Tip = -> Fillet019
FEATURE [Part::Refine] Body006001  label="LateralA_REFINADO"
  Source = -> Body006
FEATURE [App::DocumentObjectGroup] Group  label="Impresion_Refinado"
  Group = -> [Body007002,Body006001,Body007003]
FEATURE [PartDesign::ShapeBinder] ShapeBinder009  label="Taladro_posicional_001"
  Placement = pos=(-5.5,-4.5,-1e-15) rot=(0.57735,-0.57735,-0.57735;2.0944rad)
  Support = -> [Sketch059]
  TraceSupport = false
FEATURE [PartDesign::Pocket] Pocket035
  BaseFeature = -> Pocket034
  Length = 5
  Length2 = 100
  Placement = pos=(0,-4.5,-1e-15) rot=(0,0,1;0rad)
  Profile = -> ShapeBinder009
  Type = 1
FEATURE [Sketcher::SketchObject] Sketch060  label="Posicionamiento_taladros"
  ExternalGeometry = -> [Pocket035]
  FullyConstrained = true
  MapMode = 5
  Placement = pos=(-1.5,-4.5,-1e-15) rot=(0.57735,-0.57735,-0.57735;2.0944rad)
  Support = -> [Pocket035]
  constraints (4):
    c: DistanceX(g-4,g-8) = 10.5
    c: DistanceY(g-4,g-8) = -5
    c: DistanceX(g-3,g-6) = 8.25
    c: DistanceY(g-3,g-6) = 6.79618
FEATURE [PartDesign::Body] Body003  label="Placa_electronica"
  Group = -> [ShapeBinder003,Sketch022,Pad009,Sketch023,Pocket011,ShapeBinder008,Pocket034,ShapeBinder009,Pocket035,Sketch060]
  Origin = -> Origin003
  Tip = -> Pocket035
FEATURE [TechDraw::DrawSVGTemplate] Template
  EditableTexts = Designed_by_Name=A4I; Drawing_number=Drawing number; FC-Date=5/3/2022; FC-SC=Scale; FC-SH=Sheet; FC-Title=Habitáculo Pila; Subtitle=Subtitle; Weight=Weight
  Height = 210
  Orientation = 1
  Width = 297
FEATURE [TechDraw::DrawProjGroupItem] ProjItem  label="Front"
  CoarseView = false
  Direction = (0,1,0)
  Focus = 100
  HardHidden = false
  IsoCount = 0
  IsoHidden = false
  IsoVisible = false
  LockPosition = true
  Perspective = false
  Rotation = 0
  RotationVector = (-1,0,0)
  ScaleType = 2
  SeamHidden = false
  SeamVisible = true
  SmoothHidden = false
  SmoothVisible = true
  Source = -> [Body]
  Type = 0
  X = 0
  XDirection = (-1,0,0)
  Y = 0
FEATURE [TechDraw::DrawProjGroupItem] ProjItem002  label="Top"
  CoarseView = false
  Direction = (0,0,1)
  Focus = 100
  HardHidden = false
  IsoCount = 0
  IsoHidden = false
  IsoVisible = false
  LockPosition = false
  Perspective = false
  Rotation = 0
  RotationVector = (1,0,0)
  ScaleType = 2
  SeamHidden = false
  SeamVisible = true
  SmoothHidden = false
  SmoothVisible = true
  Source = -> [Body]
  Type = 4
  X = 0
  XDirection = (-1,0,0)
  Y = -85.5
FEATURE [TechDraw::DrawProjGroup] ProjGroup
  Anchor = -> ProjItem
  AutoDistribute = true
  LockPosition = false
  ProjectionType = 0
  Rotation = 0
  ScaleType = 0
  Source = -> [Body]
  Views = -> [ProjItem,ProjItem002]
  X = 66.3404
  Y = 158.239
  spacingX = 15
  spacingY = 15
FEATURE [TechDraw::DrawViewDimension] Dimension
  Arbitrary = false
  ArbitraryTolerances = false
  EqualTolerance = true
  FormatSpec = %.2f
  FormatSpecOverTolerance = %+.2f
  FormatSpecUnderTolerance = %+.2f
  Inverted = false
  LockPosition = false
  MeasureType = 1
  OverTolerance = 0
  References2D = -> [ProjItem002]
  Rotation = 0
  ScaleType = 0
  TheoreticalExact = false
  Type = 2
  UnderTolerance = 0
  X = 42.1486
  Y = 0
FEATURE [TechDraw::DrawViewDimension] Dimension001
  Arbitrary = false
  ArbitraryTolerances = false
  EqualTolerance = true
  FormatSpec = %.2f
  FormatSpecOverTolerance = %+.2f
  FormatSpecUnderTolerance = %+.2f
  Inverted = false
  LockPosition = false
  MeasureType = 1
  OverTolerance = 0
  References2D = -> [ProjItem002]
  Rotation = 0
  ScaleType = 0
  TheoreticalExact = false
  Type = 1
  UnderTolerance = 0
  X = -1.09546
  Y = -44.5614
FEATURE [TechDraw::DrawViewDimension] Dimension003
  Arbitrary = false
  ArbitraryTolerances = false
  EqualTolerance = true
  FormatSpec = %.2f
  FormatSpecOverTolerance = %+.2f
  FormatSpecUnderTolerance = %+.2f
  Inverted = false
  LockPosition = false
  MeasureType = 1
  OverTolerance = 0
  References2D = -> [ProjItem]
  Rotation = 0
  ScaleType = 0
  TheoreticalExact = false
  Type = 2
  UnderTolerance = 0
  X = -40.7256
  Y = 1.56002
FEATURE [TechDraw::DrawViewBalloon] Balloon
  BubbleShape = 3
  EndType = 0
  EndTypeScale = 1
  KinkLength = 5
  LockPosition = false
  OriginX = 8.95916
  OriginY = -13.91
  Rotation = 0
  ScaleType = 0
  ShapeScale = 1
  SourceView = -> ProjItem
  Text = Pilas
  TextWrapLen = -1
  X = 37.3593
  Y = 6.08998
FEATURE [TechDraw::DrawViewBalloon] Balloon001
  BubbleShape = 3
  EndType = 3
  EndTypeScale = 0.5
  KinkLength = 5
  LockPosition = false
  OriginX = -0.340978
  OriginY = -9.40995
  Rotation = 0
  ScaleType = 0
  ShapeScale = 1
  SourceView = -> ProjItem
  Text = Antena 868MHz
  TextWrapLen = -1
  X = -0.44128
  Y = -38.0107
FEATURE [TechDraw::DrawViewBalloon] Balloon002
  BubbleShape = 3
  EndType = 0
  EndTypeScale = 1
  KinkLength = 5
  LockPosition = false
  OriginX = -17.7412
  OriginY = 10.9904
  Rotation = 0
  ScaleType = 0
  ShapeScale = 1
  SourceView = -> ProjItem
  Text = GPS
  TextWrapLen = -1
  X = 15.159
  Y = 27.6903
FEATURE [TechDraw::DrawViewBalloon] Balloon003
  BubbleShape = 6
  EndType = 0
  EndTypeScale = 1
  KinkLength = 5
  LockPosition = false
  OriginX = 0.85904
  OriginY = -1.60983
  Rotation = 0
  ScaleType = 0
  ShapeScale = 1
  SourceView = -> ProjItem
  Text = Anclaje placa electrónica
  TextWrapLen = -1
  X = 32.8592
  Y = 17.7902
FEATURE [TechDraw::DrawPage] Page  label="Habitáculo Pila"
  KeepUpdated = true
  NextBalloonIndex = 6
  ProjectionType = 0
  Template = -> Template
  Views = -> [ProjGroup,Dimension,Dimension001,Dimension003,Balloon,Balloon001,Balloon002,Balloon003]
FEATURE [TechDraw::DrawSVGTemplate] Template001
  EditableTexts = Designed_by_Name=Designed by Name; Drawing_number=Drawing number; FC-Date=Date; FC-SC=Scale; FC-SH=Sheet; FC-Title=Title; Subtitle=Subtitle; Weight=Weight
  Height = 210
  Orientation = 1
  Width = 297
FEATURE [TechDraw::DrawViewPart] View
  CoarseView = false
  Direction = (0,-1,0)
  Focus = 100
  HardHidden = false
  IsoCount = 0
  IsoHidden = false
  IsoVisible = false
  LockPosition = false
  Perspective = false
  Rotation = 0
  ScaleType = 0
  SeamHidden = false
  SeamVisible = true
  SmoothHidden = false
  SmoothVisible = true
  Source = -> [Body009]
  X = 64.3685
  XDirection = (1,0,0)
  Y = 155.939
FEATURE [TechDraw::DrawViewPart] View001
  CoarseView = false
  Direction = (0,1,0)
  Focus = 100
  HardHidden = false
  IsoCount = 0
  IsoHidden = false
  IsoVisible = false
  LockPosition = false
  Perspective = false
  Rotation = 0
  ScaleType = 0
  SeamHidden = false
  SeamVisible = true
  SmoothHidden = false
  SmoothVisible = true
  Source = -> [Body006]
  X = 146.528
  XDirection = (-1,0,0)
  Y = 156.596
FEATURE [TechDraw::DrawViewPart] View002
  CoarseView = false
  Direction = (0,0,1)
  Focus = 100
  HardHidden = false
  IsoCount = 0
  IsoHidden = false
  IsoVisible = false
  LockPosition = false
  Perspective = false
  Rotation = 0
  ScaleType = 0
  SeamHidden = false
  SeamVisible = true
  SmoothHidden = false
  SmoothVisible = true
  Source = -> [Body006]
  X = 147.185
  XDirection = (1,0,0)
  Y = 101.714
FEATURE [TechDraw::DrawViewPart] View003
  CoarseView = false
  Direction = (0,0,1)
  Focus = 100
  HardHidden = false
  IsoCount = 0
  IsoHidden = false
  IsoVisible = false
  LockPosition = false
  Perspective = false
  Rotation = 0
  ScaleType = 0
  SeamHidden = false
  SeamVisible = true
  SmoothHidden = false
  SmoothVisible = true
  Source = -> [Body009]
  X = 65.3545
  XDirection = (1,0,0)
  Y = 97.4413
FEATURE [TechDraw::DrawViewPart] View004
  CoarseView = false
  Direction = (0,0,1)
  Focus = 100
  HardHidden = false
  IsoCount = 0
  IsoHidden = false
  IsoVisible = false
  LockPosition = false
  Perspective = false
  Rotation = 0
  ScaleType = 0
  SeamHidden = false
  SeamVisible = true
  SmoothHidden = false
  SmoothVisible = true
  Source = -> [Body007]
  X = 230.66
  XDirection = (1,0,0)
  Y = 155.939
FEATURE [TechDraw::DrawViewPart] View005
  CoarseView = false
  Direction = (0,-1,0)
  Focus = 100
  HardHidden = false
  IsoCount = 0
  IsoHidden = false
  IsoVisible = false
  LockPosition = false
  Perspective = false
  Rotation = 0
  ScaleType = 0
  SeamHidden = false
  SeamVisible = true
  SmoothHidden = false
  SmoothVisible = true
  Source = -> [Body007]
  X = 231.646
  XDirection = (1,0,0)
  Y = 120.446
FEATURE [TechDraw::DrawViewBalloon] Balloon004
  BubbleShape = 0
  EndType = 0
  EndTypeScale = 1
  KinkLength = 5
  LockPosition = false
  OriginX = -26.2465
  OriginY = 6.07981
  Rotation = 0
  ScaleType = 0
  ShapeScale = 1
  SourceView = -> View
  Text = 1
  TextWrapLen = -1
  X = -45.6831
  Y = 30.0235
FEATURE [TechDraw::DrawViewBalloon] Balloon005
  BubbleShape = 0
  EndType = 0
  EndTypeScale = 1
  KinkLength = 5
  LockPosition = false
  OriginX = 19.7629
  OriginY = 14.6244
  Rotation = 0
  ScaleType = 0
  ShapeScale = 1
  SourceView = -> View001
  Text = 2
  TextWrapLen = -1
  X = 43.3779
  Y = 30.6808
FEATURE [TechDraw::DrawViewBalloon] Balloon006
  BubbleShape = 0
  EndType = 0
  EndTypeScale = 1
  KinkLength = 5
  LockPosition = false
  OriginX = 8.91784
  OriginY = -11.0094
  Rotation = 0
  ScaleType = 0
  ShapeScale = 1
  SourceView = -> View001
  Text = 3
  TextWrapLen = -1
  X = 42.392
  Y = 18.8498
FEATURE [TechDraw::DrawViewBalloon] Balloon007
  BubbleShape = 0
  EndType = 0
  EndTypeScale = 1
  KinkLength = 5
  LockPosition = false
  OriginX = 10.8897
  OriginY = 2.13615
  Rotation = 0
  ScaleType = 0
  ShapeScale = 1
  SourceView = -> View003
  Text = 4
  TextWrapLen = -1
  X = 30.8897
  Y = 15.2347
FEATURE [TechDraw::DrawViewBalloon] Balloon008
  BubbleShape = 0
  EndType = 0
  EndTypeScale = 1
  KinkLength = 5
  LockPosition = false
  OriginX = 20.7488
  OriginY = -3.4507
  Rotation = 0
  ScaleType = 0
  ShapeScale = 1
  SourceView = -> View005
  Text = 5
  TextWrapLen = -1
  X = 35.4906
  Y = -22.5587
FEATURE [TechDraw::DrawViewBalloon] Balloon009
  BubbleShape = 0
  EndType = 0
  EndTypeScale = 1
  KinkLength = 5
  LockPosition = false
  OriginX = -1.26995
  OriginY = 2.79343
  Rotation = 0
  ScaleType = 0
  ShapeScale = 1
  SourceView = -> View
  Text = 6
  TextWrapLen = -1
  X = 26.946
  Y = 38.2394
FEATURE [TechDraw::DrawViewBalloon] Balloon010
  BubbleShape = 0
  EndType = 0
  EndTypeScale = 1
  KinkLength = 5
  LockPosition = false
  OriginX = 55.9131
  OriginY = -12.9812
  Rotation = 0
  ScaleType = 0
  ShapeScale = 1
  SourceView = -> View
  Text = 7
  TextWrapLen = -1
  X = 75.9131
  Y = 7.01878
FEATURE [TechDraw::DrawViewBalloon] Balloon011
  BubbleShape = 0
  EndType = 0
  EndTypeScale = 1
  KinkLength = 5
  LockPosition = false
  OriginX = -24.2746
  OriginY = -13.6385
  Rotation = 0
  ScaleType = 0
  ShapeScale = 1
  SourceView = -> View001
  Text = 8
  TextWrapLen = -1
  X = -40.0962
  Y = -25.1878
FEATURE [TechDraw::DrawViewBalloon] Balloon012
  BubbleShape = 0
  EndType = 0
  EndTypeScale = 1
  KinkLength = 5
  LockPosition = false
  OriginX = -20.9883
  OriginY = 3.4507
  Rotation = 0
  ScaleType = 0
  ShapeScale = 1
  SourceView = -> View004
  Text = 9
  TextWrapLen = -1
  X = -0.988263
  Y = 18.5211
FEATURE [TechDraw::DrawViewPart] View006
  CoarseView = false
  Direction = (0,0,1)
  Focus = 100
  HardHidden = false
  IsoCount = 0
  IsoHidden = false
  IsoVisible = false
  LockPosition = false
  Perspective = false
  Rotation = 0
  ScaleType = 0
  SeamHidden = false
  SeamVisible = true
  SmoothHidden = false
  SmoothVisible = true
  Source = -> [Body004]
  X = 263.195
  XDirection = (1,0,0)
  Y = 186.502
FEATURE [TechDraw::DrawViewBalloon] Balloon013
  BubbleShape = 0
  EndType = 0
  EndTypeScale = 1
  KinkLength = 5
  LockPosition = false
  OriginX = -2.25587
  OriginY = -0.164319
  Rotation = 0
  ScaleType = 0
  ShapeScale = 1
  SourceView = -> View006
  Text = 10
  TextWrapLen = -1
  X = -23.993
  Y = 5.04695
FEATURE [TechDraw::DrawPage] Page001
  KeepUpdated = true
  NextBalloonIndex = 11
  ProjectionType = 0
  Template = -> Template001
  Views = -> [View,View001,View002,View003,View004,View005,Balloon004,Balloon005,Balloon006,Balloon007,Balloon008,Balloon009,Balloon010,Balloon011,Balloon012,View006,Balloon013]
FEATURE [TechDraw::DrawSVGTemplate] Template002
  EditableTexts = Designed_by_Name=Designed by Name; Drawing_number=Drawing number; FC-Date=Date; FC-SC=Scale; FC-SH=Sheet; FC-Title=Title; Subtitle=Subtitle; Weight=Weight
  Height = 210
  Orientation = 1
  Width = 297
FEATURE [TechDraw::DrawViewPart] View007
  CoarseView = false
  Direction = (0.577,-0.577,0.577)
  Focus = 100
  HardHidden = false
  IsoCount = 0
  IsoHidden = false
  IsoVisible = false
  LockPosition = false
  Perspective = false
  Rotation = 0
  ScaleType = 0
  SeamHidden = false
  SeamVisible = true
  SmoothHidden = false
  SmoothVisible = true
  Source = -> [Body,Body009,Body007,Body006,Body005,Body003,Body004]
  X = 101.833
  XDirection = (0.707,0.707,0)
  Y = 128.005
FEATURE [TechDraw::DrawViewDimension] Dimension004
  Arbitrary = true
  ArbitraryTolerances = false
  EqualTolerance = true
  FormatSpec = 115
  FormatSpecOverTolerance = %+.2f
  FormatSpecUnderTolerance = %+.2f
  Inverted = false
  LockPosition = false
  MeasureType = 1
  OverTolerance = 0
  References2D = -> [View007]
  Rotation = 0
  ScaleType = 0
  TheoreticalExact = false
  Type = 0
  UnderTolerance = 0
  X = 16.668
  Y = -34.5043
FEATURE [TechDraw::DrawViewDimension] Dimension005
  Arbitrary = false
  ArbitraryTolerances = false
  EqualTolerance = true
  FormatSpec = ⌀%.2f
  FormatSpecOverTolerance = %+.2f
  FormatSpecUnderTolerance = %+.2f
  Inverted = false
  LockPosition = false
  MeasureType = 1
  OverTolerance = 0
  References2D = -> [View007]
  Rotation = 0
  ScaleType = 0
  TheoreticalExact = false
  Type = 5
  UnderTolerance = 0
  X = -77.5039
  Y = -4.92958
FEATURE [TechDraw::DrawPage] Page002  label="Perspectiva"
  KeepUpdated = true
  NextBalloonIndex = 1
  ProjectionType = 0
  Template = -> Template002
  Views = -> [View007,Dimension004,Dimension005]
